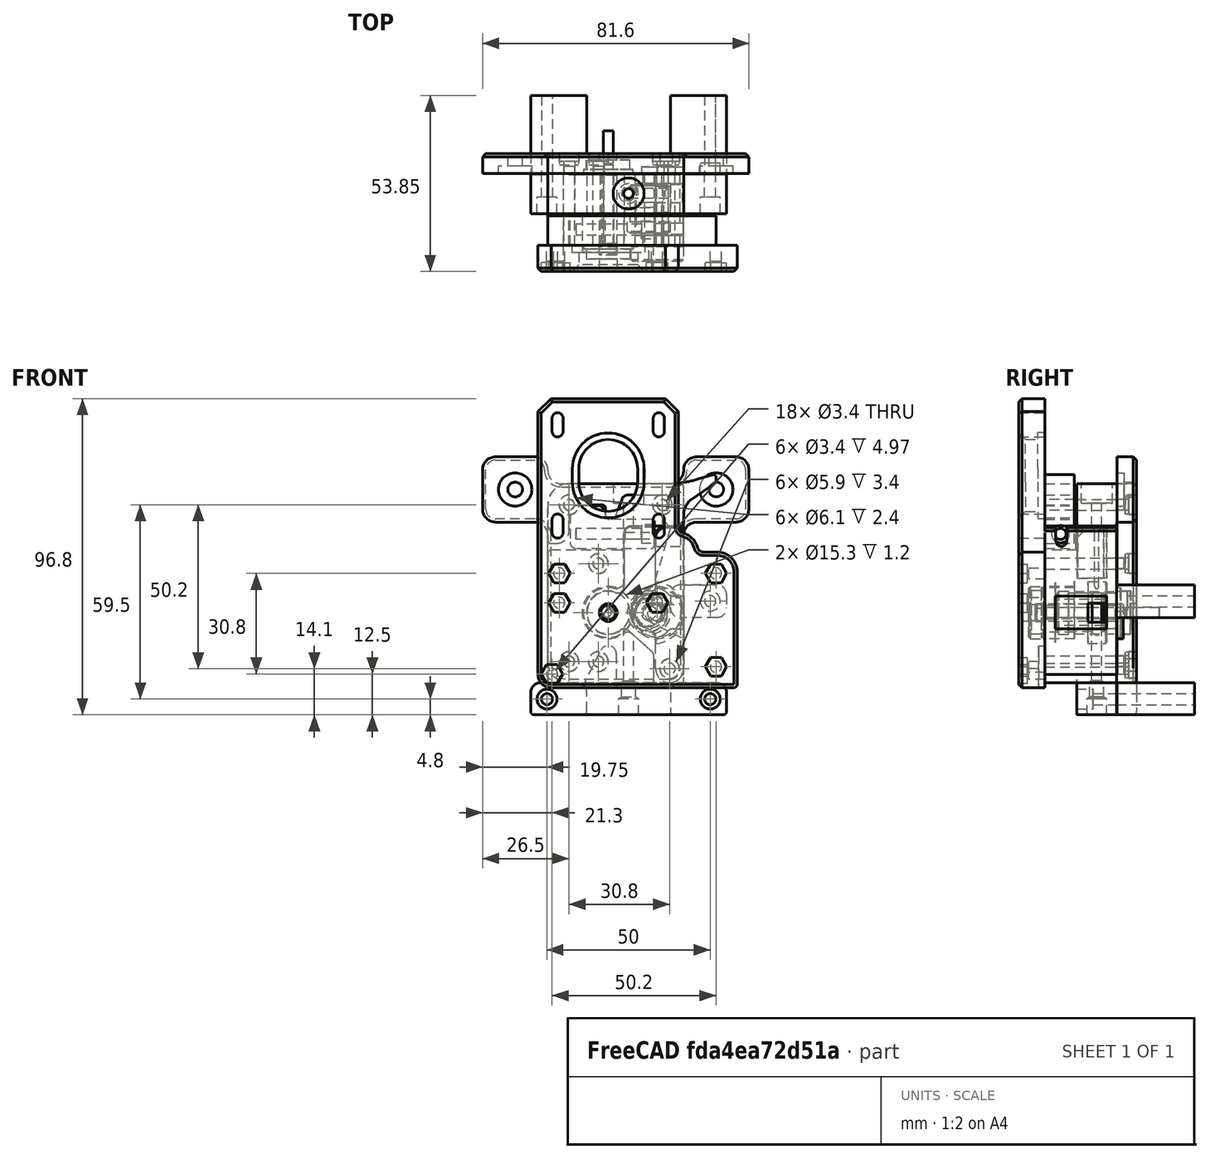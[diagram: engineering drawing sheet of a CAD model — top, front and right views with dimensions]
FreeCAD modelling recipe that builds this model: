
FCSTD DOCUMENT  (FreeCAD 1.0R39319 (Git))
Label: belted_extruder_v0.4
License: All rights reserved
LicenseURL: https://en.wikipedia.org/wiki/All_rights_reserved
objects: Sketcher::SketchObject×54, PartDesign::Fillet×34, PartDesign::Pad×26, PartDesign::Pocket×26, PartDesign::SubShapeBinder×15, PartDesign::Body×14, PartDesign::Hole×14, PartDesign::Chamfer×13, App::Part×13, App::DocumentObjectGroup×4, App::Link×4, App::FeaturePython×4, Mesh::Feature×2, PartDesign::Plane×2, PartDesign::Revolution×1, Spreadsheet::Sheet×1, PartDesign::FeatureBase×1, Assembly::JointGroup×1, Assembly::AssemblyObject×1
note: 483 computed .brp shape members not serialized (recipe doc carries the construction recipe); baked Part::Feature solids carry a one-line shape summary decoded from their .brp

FEATURE [Mesh::Feature] _0t_pulley_no_flange  label="60t_pulley_no_flange"
  Placement = pos=(0,-18,0) rot=(1,0,0;1.5708rad)
FEATURE [Mesh::Feature] _0t_pulley_no_flange001  label="80t_pulley_no_flange"
  Placement = pos=(0,-18,0) rot=(1,0,0;1.5708rad)
FEATURE [Sketcher::SketchObject] Sketch  label="base pulleys sketch"
  ArcFitTolerance = 1e-06
  FullyConstrained = true
  MakeInternals = false
  Placement = pos=(0,0,0) rot=(1,0,0;1.5708rad)
  sketch-geometry (12):
    g0: Circle CenterX=0 CenterY=0 CenterZ=0 NormalX=0 NormalY=0 NormalZ=1 AngleXU=0 Radius=25
    g1: Circle CenterX=-15.5 CenterY=59.5 CenterZ=0 NormalX=0 NormalY=0 NormalZ=1 AngleXU=0 Radius=1.7
    g2: Circle CenterX=15.5 CenterY=59.5 CenterZ=0 NormalX=0 NormalY=0 NormalZ=1 AngleXU=0 Radius=1.7
    g3: Circle CenterX=-15.5 CenterY=28.5 CenterZ=0 NormalX=0 NormalY=0 NormalZ=1 AngleXU=0 Radius=1.7
    g4: Circle CenterX=15.5 CenterY=28.5 CenterZ=0 NormalX=0 NormalY=0 NormalZ=1 AngleXU=0 Radius=1.7
    g5: LineSegment [constr] StartX=-15.5 StartY=59.5 StartZ=0 EndX=-15.5 EndY=28.5 EndZ=0
    g6: LineSegment [constr] StartX=-15.5 StartY=59.5 StartZ=0 EndX=15.5 EndY=59.5 EndZ=0
    g7: LineSegment [constr] StartX=15.5 StartY=59.5 StartZ=0 EndX=15.5 EndY=28.5 EndZ=0
    g8: LineSegment [constr] StartX=15.5 StartY=28.5 StartZ=0 EndX=-15.5 EndY=28.5 EndZ=0
    g9: LineSegment [constr] StartX=15.5 StartY=28.5 StartZ=0 EndX=-15.5 EndY=59.5 EndZ=0
    g10: Circle CenterX=3e-15 CenterY=44 CenterZ=0 NormalX=0 NormalY=0 NormalZ=1 AngleXU=0 Radius=9
    g11: Circle CenterX=0 CenterY=0 CenterZ=0 NormalX=0 NormalY=0 NormalZ=1 AngleXU=0 Radius=6
  constraints (27):
    c: Coincident(g0,g-1)
    c: Diameter(g0) = 50
    c: DistanceX(g1,g2) = 31
    c: DistanceY(g3,g1) = 31
    c: Coincident(g5,g1)
    c: Coincident(g5,g3)
    c: Vertical(g5)
    c: Coincident(g6,g1)
    c: Coincident(g6,g2)
    c: Coincident(g7,g2)
    c: Coincident(g7,g4)
    c: Vertical(g7)
    c: Coincident(g8,g4)
    c: Coincident(g8,g3)
    c: Horizontal(g8)
    c: Symmetric(g1,g2,g-2)
    c: Diameter(g2) = 3.4
    c: Equal(g2,g1)
    c: Equal(g3,g4)
    c: Equal(g3,g1)
    c: Coincident(g9,g4)
    c: Coincident(g9,g1)
    c: Symmetric(g9,g9,g10)
    c: Diameter(g10) = 18
    c: Coincident(g11,g0)
    c: Diameter(g11) = 12
    c: DistanceY(g0,g10) = 44
FEATURE [PartDesign::SubShapeBinder] Binder  label="base pulley binder"
  BindCopyOnChange = 0
  BindMode = 0
  ClaimChildren = false
  Context = -> Part [Body.Binder.]
  Fuse = false
  MakeFace = true
  OffsetFill = false
  OffsetIntersection = false
  OffsetJoinType = 0
  OffsetOpenResult = false
  PartialLoad = false
  Placement = pos=(0,0,0) rot=(0,-1,0;1.5708rad)
  Refine = true
  Relative = true
  Support = -> [Sketch]
  _Version = 2
FEATURE [Sketcher::SketchObject] Sketch006  label="filament path sketch"
  ArcFitTolerance = 1e-06
  FullyConstrained = true
  MakeInternals = false
  sketch-geometry (2):
    g0: Circle CenterX=6.25 CenterY=15.85 CenterZ=0 NormalX=0 NormalY=0 NormalZ=1 AngleXU=0 Radius=1.425
    g1: Circle CenterX=6.25 CenterY=15.85 CenterZ=0 NormalX=0 NormalY=0 NormalZ=1 AngleXU=0 Radius=5
  constraints (5):
    c: Diameter(g0) = 2.85
    c: DistanceX(g-1,g0) = 6.25
    c: DistanceY(g-1,g0) = 15.85
    c: Coincident(g1,g0)
    c: Diameter(g1) = 10
FEATURE [Sketcher::SketchObject] Sketch007
  ArcFitTolerance = 1e-06
  AttachmentSupport = -> [XY_Plane019]
  FullyConstrained = true
  MakeInternals = false
  MapMode = 5
  expr: Constraints[2] = 11.75 / 2
  expr: Constraints[6] = 13.25 / 2
  sketch-geometry (12):
    g0: LineSegment StartX=4 StartY=18.375 StartZ=0 EndX=5.875 EndY=18.375 EndZ=0
    g1: LineSegment [constr] StartX=0 StartY=18.375 StartZ=0 EndX=0 EndY=3.625 EndZ=0
    g2: LineSegment StartX=4 StartY=3.625 StartZ=0 EndX=6.625 EndY=3.625 EndZ=0
    g3: LineSegment StartX=6.625 StartY=3.625 StartZ=0 EndX=6.625 EndY=7.125 EndZ=0
    g4: LineSegment StartX=5.875 StartY=18.375 StartZ=0 EndX=5.875 EndY=17.375 EndZ=0
    g5: LineSegment [constr] StartX=5.875 StartY=17.375 StartZ=0 EndX=5.875 EndY=14.375 EndZ=0
    g6: LineSegment StartX=5.875 StartY=14.375 StartZ=0 EndX=5.875 EndY=7.125 EndZ=0
    g7: LineSegment StartX=5.875 StartY=7.125 StartZ=0 EndX=6.625 EndY=7.125 EndZ=0
    g8: ArcOfCircle CenterX=6.375 CenterY=15.875 CenterZ=0 NormalX=0 NormalY=0 NormalZ=1 AngleXU=0 Radius=1.58114 StartAngle=1.89255 EndAngle=4.39064
    g9: LineSegment StartX=4 StartY=18.375 StartZ=0 EndX=4 EndY=3.625 EndZ=0
    g10: LineSegment [constr] StartX=0 StartY=18.375 StartZ=0 EndX=4 EndY=18.375 EndZ=0
    g11: LineSegment [constr] StartX=0 StartY=3.625 StartZ=0 EndX=4 EndY=3.625 EndZ=0
  constraints (35):
    c: PointOnObject(g1,g-2)
    c: Horizontal(g0)
    c: DistanceX(g1,g0) = 5.875
    c: PointOnObject(g1,g-2)
    c: DistanceY(g1,g1) = 14.75
    c: Horizontal(g2)
    c: DistanceX(g1,g2) = 6.625
    c: Coincident(g3,g2)
    c: Vertical(g3)
    c: DistanceY(g3,g3) = 3.5
    c: Coincident(g4,g0)
    c: Vertical(g4)
    c: Coincident(g5,g4)
    c: Vertical(g5)
    c: DistanceY(g4,g4) = 1
    c: DistanceY(g5,g5) = 3
    c: Coincident(g6,g5)
    c: Vertical(g6)
    c: Coincident(g7,g6)
    c: Coincident(g7,g3)
    c: Horizontal(g7)
    c: DistanceY(g-1,g1) = 3.625
    c: Coincident(g8,g4)
    c: Coincident(g8,g5)
    c: DistanceX(g4,g8) = 0.5
    c: Vertical(g9)
    c: DistanceX(g1,g9) = 4
    c: Coincident(g0,g9)
    c: Coincident(g2,g9)
    c: Coincident(g10,g1)
    c: Coincident(g10,g0)
    c: Horizontal(g10)
    c: Coincident(g11,g1)
    c: Coincident(g11,g2)
    c: Horizontal(g11)
FEATURE [PartDesign::Revolution] Revolution
  Angle = 360
  Angle2 = 60
  Axis = (0,1,0)
  Base = (0,0,0)
  Profile = -> Sketch007
  ReferenceAxis = -> Sketch007 [V_Axis]
  Refine = true
  Reversed = true
  Suppressed = false
  Type = 0
FEATURE [PartDesign::Chamfer] Chamfer003
  Angle = 45
  Base = -> Revolution [Edge1,Edge2]
  BaseFeature = -> Revolution
  ChamferType = 0
  FlipDirection = false
  Refine = true
  Size = 0.25
  Size2 = 1
  SupportTransform = false
  Suppressed = false
  UseAllEdges = false
FEATURE [PartDesign::Chamfer] Chamfer004
  Angle = 45
  Base = -> Chamfer003 [Edge11]
  BaseFeature = -> Chamfer003
  ChamferType = 1
  FlipDirection = false
  Refine = true
  Size = 1
  Size2 = 0.5
  SupportTransform = false
  Suppressed = false
  UseAllEdges = false
FEATURE [PartDesign::Body] Body001  label="Drive Gear Body"
  AllowCompound = false
  Group = -> [Sketch007,Revolution,Chamfer003,Chamfer004]
  Origin = -> Origin019
  Tip = -> Chamfer004
FEATURE [PartDesign::SubShapeBinder] Binder003  label="filament path binder001"
  BindCopyOnChange = 0
  BindMode = 0
  ClaimChildren = false
  Context = -> Part003 [Body003.Binder003.]
  Fuse = false
  MakeFace = true
  OffsetFill = false
  OffsetIntersection = false
  OffsetJoinType = 0
  OffsetOpenResult = false
  PartialLoad = false
  Refine = true
  Relative = true
  Support = -> [Sketch006]
  _Version = 2
FEATURE [Sketcher::SketchObject] Sketch014  label="body screw placement"
  ArcFitTolerance = 1e-06
  FullyConstrained = true
  MakeInternals = false
  Placement = pos=(0,0,0) rot=(1,0,0;1.5708rad)
  sketch-geometry (15):
    g0: Circle CenterX=18.8 CenterY=-17.2 CenterZ=0 NormalX=0 NormalY=0 NormalZ=1 AngleXU=0 Radius=1.7
    g1: Circle CenterX=0 CenterY=33 CenterZ=0 NormalX=0 NormalY=0 NormalZ=1 AngleXU=0 Radius=1.7
    g2: Circle CenterX=-12 CenterY=33 CenterZ=0 NormalX=0 NormalY=0 NormalZ=1 AngleXU=0 Radius=1.7
    g3: Circle CenterX=-12 CenterY=-15 CenterZ=0 NormalX=0 NormalY=0 NormalZ=1 AngleXU=0 Radius=1.7
    g4: Circle [constr] CenterX=-12 CenterY=-15 CenterZ=0 NormalX=0 NormalY=0 NormalZ=1 AngleXU=0 Radius=2.75
    g5: Circle [constr] CenterX=0 CenterY=33 CenterZ=0 NormalX=0 NormalY=0 NormalZ=1 AngleXU=0 Radius=2.75
    g6: LineSegment [constr] StartX=-12 StartY=33 StartZ=0 EndX=0 EndY=33 EndZ=0
    g7: LineSegment [constr] StartX=-12 StartY=33 StartZ=0 EndX=-12 EndY=-15 EndZ=0
    g8: Circle CenterX=-3 CenterY=15 CenterZ=0 NormalX=0 NormalY=0 NormalZ=1 AngleXU=0 Radius=1.7
    g9: Circle CenterX=-3 CenterY=-15 CenterZ=0 NormalX=0 NormalY=0 NormalZ=1 AngleXU=0 Radius=1.7
    g10: LineSegment [constr] StartX=-3 StartY=-15 StartZ=0 EndX=-12 EndY=-15 EndZ=0
    g11: Circle CenterX=16.6 CenterY=33 CenterZ=0 NormalX=0 NormalY=0 NormalZ=1 AngleXU=0 Radius=1.7
    g12: LineSegment [constr] StartX=0 StartY=33 StartZ=0 EndX=16.6 EndY=33 EndZ=0
    g13: LineSegment [constr] StartX=18.8 StartY=-17.2 StartZ=0 EndX=18.8 EndY=33 EndZ=0
    g14: LineSegment [constr] StartX=16.6 StartY=33 StartZ=0 EndX=18.8 EndY=33 EndZ=0
  constraints (37):
    c: Diameter(g3) = 3.4
    c: Equal(g3,g2)
    c: Equal(g2,g1)
    c: Equal(g1,g0)
    c: Coincident(g4,g3)
    c: Diameter(g4) = 5.5
    c: Coincident(g5,g1)
    c: Diameter(g5) = 5.5
    c: Coincident(g6,g2)
    c: Coincident(g6,g1)
    c: Horizontal(g6)
    c: Coincident(g7,g2)
    c: Coincident(g7,g3)
    c: Vertical(g7)
    c: DistanceX(g2,g-1) = 12
    c: DistanceX(g-1,g0) = 18.8
    c: DistanceY(g-1,g2) = 33
    c: DistanceY(g3,g-1) = 15
    c: DistanceX(g-1,g1) = 0
    c: Coincident(g10,g9)
    c: Coincident(g10,g3)
    c: Horizontal(g10)
    c: Equal(g9,g3)
    c: Equal(g8,g9)
    c: DistanceY(g0,g9) = 2.2
    c: Symmetric(g9,g8,g-1)
    c: DistanceX(g8,g-1) = 3
    c: Coincident(g12,g1)
    c: Coincident(g12,g11)
    c: Horizontal(g12)
    c: Coincident(g13,g0)
    c: Vertical(g13)
    c: Coincident(g14,g11)
    c: Coincident(g14,g13)
    c: Horizontal(g14)
    c: DistanceX(g11,g13) = 2.2
    c: Equal(g3,g11)
FEATURE [PartDesign::SubShapeBinder] Binder004  label="tensioner axel binder"
  BindCopyOnChange = 0
  BindMode = 0
  ClaimChildren = false
  Context = -> Part003 [Body003.Binder004.]
  Fuse = false
  MakeFace = true
  OffsetFill = false
  OffsetIntersection = false
  OffsetJoinType = 0
  OffsetOpenResult = false
  PartialLoad = false
  Refine = true
  Relative = true
  Support = -> [Sketch014]
  _Version = 2
FEATURE [Sketcher::SketchObject] Sketch013  label="tensioner base sketch"
  ArcFitTolerance = 1e-06
  AttachmentSupport = -> [XZ_Plane022]
  ExternalGeometry = -> [Binder004]
  FullyConstrained = true
  MakeInternals = false
  MapMode = 5
  Placement = pos=(0,0,0) rot=(1,0,0;1.5708rad)
  sketch-geometry (15):
    g0: Circle [constr] CenterX=12.7 CenterY=0 CenterZ=0 NormalX=0 NormalY=0 NormalZ=1 AngleXU=0 Radius=4.5
    g1: LineSegment StartX=14.55 StartY=4.5 StartZ=0 EndX=14.55 EndY=26 EndZ=0
    g2: LineSegment StartX=14.55 StartY=26 StartZ=0 EndX=23.05 EndY=26 EndZ=0
    g3: Circle CenterX=12.7 CenterY=0 CenterZ=0 NormalX=0 NormalY=0 NormalZ=1 AngleXU=0 Radius=2.1
    g4: LineSegment StartX=14.55 StartY=-17.2 StartZ=0 EndX=14.55 EndY=-6.2 EndZ=0
    g5: LineSegment StartX=23.05 StartY=26 StartZ=0 EndX=23.05 EndY=-17.2 EndZ=0
    g6: LineSegment StartX=10.4965 StartY=-3.92361 StartZ=0 EndX=14.55 EndY=-6.2 EndZ=0
    g7: LineSegment [constr] StartX=14.55 StartY=-6.2 StartZ=0 EndX=14.55 EndY=4.5 EndZ=0
    g8: LineSegment StartX=14.55 StartY=4.5 StartZ=0 EndX=12.7 EndY=4.5 EndZ=0
    g9: ArcOfCircle CenterX=12.7 CenterY=0 CenterZ=0 NormalX=0 NormalY=0 NormalZ=1 AngleXU=0 Radius=4.5 StartAngle=1.5708 EndAngle=4.20069
    g10: Circle [constr] CenterX=12.7 CenterY=0 CenterZ=0 NormalX=0 NormalY=0 NormalZ=1 AngleXU=0 Radius=6
    g11: ArcOfCircle CenterX=18.8 CenterY=-17.2 CenterZ=0 NormalX=0 NormalY=0 NormalZ=1 AngleXU=0 Radius=4.25 StartAngle=3.14159 EndAngle=5.49779
    g12: ArcOfCircle [constr] CenterX=18.8 CenterY=-17.2 CenterZ=0 NormalX=0 NormalY=0 NormalZ=1 AngleXU=0 Radius=4.25 StartAngle=5.49779 EndAngle=6.28319
    g13: LineSegment StartX=23.05 StartY=-18.9604 StartZ=0 EndX=21.8052 EndY=-20.2052 EndZ=0
    g14: LineSegment StartX=23.05 StartY=-18.9604 StartZ=0 EndX=23.05 EndY=-17.2 EndZ=0
  constraints (36):
    c: PointOnObject(g0,g-1)
    c: Diameter(g0) = 9
    c: Vertical(g1)
    c: Coincident(g1,g2)
    c: Horizontal(g2)
    c: Coincident(g3,g0)
    c: Diameter(g3) = 4.2
    c: DistanceX(g-1,g0) = 12.7
    c: Coincident(g-4,g11)
    c: Tangent(g11,g4) = 1.5708
    c: Coincident(g5,g2)
    c: Vertical(g5)
    c: Tangent(g12,g5) = 1.5708
    c: Coincident(g6,g4)
    c: Coincident(g7,g4)
    c: Coincident(g7,g1)
    c: Vertical(g7)
    c: Vertical(g4)
    c: Coincident(g8,g1)
    c: Tangent(g8,g0) = -1.5708
    c: Horizontal(g8)
    c: Coincident(g9,g0)
    c: Coincident(g9,g8)
    c: Diameter(g10) = 12
    c: Coincident(g10,g0)
    c: Tangent(g6,g9) = -1.5708
    c: DistanceY(g11,g4) = 11
    c: Coincident(g11,g12)
    c: Coincident(g11,g12)
    c: Diameter(g11) = 8.5
    c: Angle(g5,g13) = 2.35619
    c: Tangent(g13,g11) = 1.5708
    c: Coincident(g14,g13)
    c: Coincident(g14,g5)
    c: Vertical(g14)
    c: DistanceY(g1,g-3) = 7
FEATURE [PartDesign::Pad] Pad003  label="tensioner base"
  Direction = (0,-1,2e-16)
  Length = 22
  Length2 = 10
  Placement = pos=(0,0,0) rot=(1,0,0;1.5708rad)
  Profile = -> Sketch013
  ReferenceAxis = -> Sketch013 [N_Axis]
  Refine = true
  Reversed = true
  Suppressed = false
  Type = 0
FEATURE [Sketcher::SketchObject] Sketch015
  ArcFitTolerance = 1e-06
  AttachmentSupport = -> [Pad003]
  ExternalGeometry = -> [Pad003]
  FullyConstrained = true
  MakeInternals = false
  MapMode = 5
  Placement = pos=(0,22,0) rot=(-1,0,0;1.5708rad)
  sketch-geometry (4):
    g0: ArcOfCircle CenterX=12.7 CenterY=4.9e-15 CenterZ=0 NormalX=0 NormalY=0 NormalZ=1 AngleXU=0 Radius=8 StartAngle=0.675132 EndAngle=5.60805
    g1: LineSegment StartX=18.945 StartY=5 StartZ=0 EndX=23.05 EndY=5 EndZ=0
    g2: LineSegment StartX=18.945 StartY=-5 StartZ=0 EndX=23.05 EndY=-5 EndZ=0
    g3: LineSegment StartX=23.05 StartY=5 StartZ=0 EndX=23.05 EndY=-5 EndZ=0
  constraints (11):
    c: Coincident(g0,g-3)
    c: Diameter(g0) = 16
    c: Horizontal(g1)
    c: Horizontal(g2)
    c: Symmetric(g2,g1,g-1)
    c: DistanceY(g2,g1) = 10
    c: Coincident(g0,g1)
    c: Coincident(g0,g2)
    c: Coincident(g3,g1)
    c: Coincident(g3,g2)
    c: PointOnObject(g2,g-4)
FEATURE [PartDesign::Pocket] Pocket005  label="tensioner pulley cutout"
  BaseFeature = -> Pad003
  Direction = (0,-1,-2e-16)
  Length = 18.9
  Length2 = -3.1
  Placement = pos=(0,0,0) rot=(1,0,0;1.5708rad)
  Profile = -> Sketch015
  ReferenceAxis = -> Sketch015 [N_Axis]
  Refine = true
  Suppressed = false
  Type = 4
FEATURE [PartDesign::SubShapeBinder] Binder006  label="body screws binder"
  BindCopyOnChange = 0
  BindMode = 0
  ClaimChildren = false
  Context = -> Part [Body.Binder006.]
  Fuse = false
  MakeFace = true
  OffsetFill = false
  OffsetIntersection = false
  OffsetJoinType = 0
  OffsetOpenResult = false
  PartialLoad = false
  Refine = true
  Relative = true
  Support = -> [Sketch014]
  _Version = 2
FEATURE [Sketcher::SketchObject] Sketch001
  ArcFitTolerance = 1e-06
  AttachmentSupport = -> [Binder]
  ExternalGeometry = -> [Binder,Binder006]
  FullyConstrained = true
  MakeInternals = false
  MapMode = 3
  Placement = pos=(0,0,0) rot=(0.57735,-0.57735,0.57735;2.0944rad)
  sketch-geometry (7):
    g0: LineSegment StartX=-23 StartY=21.5 StartZ=0 EndX=-23 EndY=-39.5 EndZ=0
    g1: LineSegment StartX=-23 StartY=-39.5 StartZ=0 EndX=18.5 EndY=-39.5 EndZ=0
    g2: LineSegment StartX=18.5 StartY=-39.5 StartZ=0 EndX=18.5 EndY=-21.5 EndZ=0
    g3: LineSegment StartX=18.5 StartY=-21.5 StartZ=0 EndX=65.5 EndY=-21.5 EndZ=0
    g4: LineSegment StartX=65.5 StartY=-21.5 StartZ=0 EndX=65.5 EndY=21.5 EndZ=0
    g5: LineSegment StartX=65.5 StartY=21.5 StartZ=0 EndX=-23 EndY=21.5 EndZ=0
    g6: Circle [constr] CenterX=44 CenterY=6.7e-15 CenterZ=0 NormalX=0 NormalY=0 NormalZ=1 AngleXU=0 Radius=21.5
  constraints (21):
    c: Vertical(g0)
    c: Coincident(g0,g1)
    c: Coincident(g1,g2)
    c: Vertical(g2)
    c: Coincident(g2,g3)
    c: Horizontal(g3)
    c: Coincident(g3,g4)
    c: Coincident(g4,g5)
    c: Coincident(g5,g0)
    c: Horizontal(g5)
    c: Symmetric(g4,g3,g-1)
    c: DistanceY(g4,g4) = 43
    c: Coincident(g6,g-3)
    c: Tangent(g6,g5)
    c: Tangent(g6,g4)
    c: DistanceX(g0,g-1) = 23
    c: Perpendicular(g2,g1)
    c: DistanceX(g-6,g1) = 6.5
    c: DistanceY(g1,g-6) = 6.5
    c: DistanceX(g-1,g6) = 44
    c: DistanceY(g2,g2) = 18
FEATURE [PartDesign::Pad] Pad
  Direction = (0,-1,0)
  Length = 8
  Length2 = 10
  Placement = pos=(0,0,0) rot=(0,-1,0;1.5708rad)
  Profile = -> Sketch001
  ReferenceAxis = -> Sketch001 [N_Axis]
  Refine = true
  Suppressed = false
  Type = 0
FEATURE [Sketcher::SketchObject] Sketch002  label="motor cutouts"
  ArcFitTolerance = 1e-06
  AttachmentSupport = -> [Pad]
  ExternalGeometry = -> [Binder]
  FullyConstrained = true
  MakeInternals = false
  MapMode = 5
  Placement = pos=(0,0,0) rot=(0.57735,-0.57735,-0.57735;4.18879rad)
  sketch-geometry (29):
    g0: ArcOfCircle CenterX=-44 CenterY=6.7e-15 CenterZ=0 NormalX=0 NormalY=0 NormalZ=1 AngleXU=0 Radius=9 StartAngle=1.5708 EndAngle=4.71239
    g1: LineSegment StartX=-44 StartY=9 StartZ=0 EndX=-40 EndY=9 EndZ=0
    g2: LineSegment StartX=-44 StartY=-9 StartZ=0 EndX=-40 EndY=-9 EndZ=0
    g3: LineSegment [constr] StartX=-44 StartY=-9 StartZ=0 EndX=-44 EndY=9 EndZ=0
    g4: ArcOfCircle CenterX=-40 CenterY=7.1e-15 CenterZ=0 NormalX=0 NormalY=0 NormalZ=1 AngleXU=0 Radius=9 StartAngle=4.71239 EndAngle=7.85398
    g5: ArcOfCircle CenterX=-59.5 CenterY=15.5 CenterZ=0 NormalX=0 NormalY=0 NormalZ=1 AngleXU=0 Radius=1.7 StartAngle=1.5708 EndAngle=4.71239
    g6: ArcOfCircle CenterX=-59.5 CenterY=-15.5 CenterZ=0 NormalX=0 NormalY=0 NormalZ=1 AngleXU=0 Radius=1.7 StartAngle=1.5708 EndAngle=4.71239
    g7: ArcOfCircle CenterX=-28.5 CenterY=-15.5 CenterZ=0 NormalX=0 NormalY=0 NormalZ=1 AngleXU=0 Radius=1.7 StartAngle=1.5708 EndAngle=4.71238
    g8: ArcOfCircle CenterX=-28.5 CenterY=15.5 CenterZ=0 NormalX=0 NormalY=0 NormalZ=1 AngleXU=0 Radius=1.7 StartAngle=1.5708 EndAngle=4.71239
    g9: LineSegment StartX=-59.5 StartY=13.8 StartZ=0 EndX=-55.5 EndY=13.8 EndZ=0
    g10: LineSegment StartX=-59.5 StartY=17.2 StartZ=0 EndX=-55.5 EndY=17.2 EndZ=0
    g11: LineSegment [constr] StartX=-59.5 StartY=17.2 StartZ=0 EndX=-59.5 EndY=13.8 EndZ=0
    g12: LineSegment [constr] StartX=-55.5 StartY=17.2 StartZ=0 EndX=-55.5 EndY=13.8 EndZ=0
    g13: ArcOfCircle CenterX=-55.5 CenterY=15.5 CenterZ=0 NormalX=0 NormalY=0 NormalZ=1 AngleXU=0 Radius=1.7 StartAngle=4.71239 EndAngle=7.85398
    g14: LineSegment StartX=-59.5 StartY=-13.8 StartZ=0 EndX=-55.5 EndY=-13.8 EndZ=0
    g15: LineSegment StartX=-59.5 StartY=-17.2 StartZ=0 EndX=-55.5 EndY=-17.2 EndZ=0
    g16: LineSegment [constr] StartX=-59.5 StartY=-13.8 StartZ=0 EndX=-59.5 EndY=-17.2 EndZ=0
    g17: LineSegment [constr] StartX=-55.5 StartY=-13.8 StartZ=0 EndX=-55.5 EndY=-17.2 EndZ=0
    g18: ArcOfCircle CenterX=-55.5 CenterY=-15.5 CenterZ=0 NormalX=0 NormalY=0 NormalZ=1 AngleXU=0 Radius=1.7 StartAngle=4.71238 EndAngle=7.85399
    g19: LineSegment StartX=-28.5 StartY=-17.2 StartZ=0 EndX=-24.5 EndY=-17.2 EndZ=0
    g20: LineSegment StartX=-28.5 StartY=-13.8 StartZ=0 EndX=-24.5 EndY=-13.8 EndZ=0
    g21: LineSegment [constr] StartX=-28.5 StartY=-13.8 StartZ=0 EndX=-28.5 EndY=-17.2 EndZ=0
    g22: LineSegment [constr] StartX=-24.5 StartY=-13.8 StartZ=0 EndX=-24.5 EndY=-17.2 EndZ=0
    g23: ArcOfCircle CenterX=-24.5 CenterY=-15.5 CenterZ=0 NormalX=0 NormalY=0 NormalZ=1 AngleXU=0 Radius=1.7 StartAngle=4.71239 EndAngle=7.85398
    g24: LineSegment StartX=-28.5 StartY=13.8 StartZ=0 EndX=-24.5 EndY=13.8 EndZ=0
    g25: LineSegment StartX=-28.5 StartY=17.2 StartZ=0 EndX=-24.5 EndY=17.2 EndZ=0
    g26: LineSegment [constr] StartX=-24.5 StartY=17.2 StartZ=0 EndX=-24.5 EndY=13.8 EndZ=0
    g27: LineSegment [constr] StartX=-28.5 StartY=17.2 StartZ=0 EndX=-28.5 EndY=13.8 EndZ=0
    g28: ArcOfCircle CenterX=-24.5 CenterY=15.5 CenterZ=0 NormalX=0 NormalY=0 NormalZ=1 AngleXU=0 Radius=1.7 StartAngle=4.71239 EndAngle=7.85398
  constraints (76):
    c: Coincident(g0,g-3)
    c: Equal(g0,g-3)
    c: Horizontal(g1)
    c: Horizontal(g2)
    c: Coincident(g3,g2)
    c: Coincident(g3,g1)
    c: Vertical(g3)
    c: DistanceX(g2,g2) = 4
    c: Coincident(g0,g1)
    c: Tangent(g0,g2) = -1.5708
    c: Coincident(g4,g1)
    c: Equal(g5,g-4)
    c: Equal(g2,g1)
    c: Coincident(g5,g-4)
    c: Coincident(g6,g-5)
    c: Coincident(g7,g-7)
    c: Equal(g-5,g6)
    c: Equal(g7,g-7)
    c: Horizontal(g9)
    c: Coincident(g11,g10)
    c: Coincident(g11,g9)
    c: Vertical(g11)
    c: Coincident(g12,g10)
    c: Coincident(g12,g9)
    c: Vertical(g12)
    c: DistanceX(g9,g9) = 4
    c: Equal(g12,g11)
    c: Symmetric(g12,g12,g13)
    c: Coincident(g13,g10)
    c: Coincident(g5,g9)
    c: Tangent(g5,g10) = 1.5708
    c: Horizontal(g14)
    c: Horizontal(g15)
    c: Coincident(g16,g14)
    c: Coincident(g16,g15)
    c: Coincident(g17,g14)
    c: Coincident(g17,g15)
    c: Vertical(g17)
    c: Vertical(g16)
    c: DistanceX(g15,g15) = 4
    c: Tangent(g6,g14) = 1.5708
    c: Coincident(g6,g15)
    c: Coincident(g18,g14)
    c: Angle(g13) = 3.14159
    c: Horizontal(g19)
    c: Horizontal(g20)
    c: Coincident(g21,g20)
    c: Coincident(g21,g19)
    c: Coincident(g7,g19)
    c: Coincident(g22,g20)
    c: Coincident(g22,g19)
    c: Vertical(g22)
    c: DistanceX(g19,g19) = 4
    c: Coincident(g23,g19)
    c: Equal(g23,g7)
    c: Coincident(g4,g2)
    c: Equal(g4,g0)
    c: Equal(g18,g6)
    c: Coincident(g18,g15)
    c: Horizontal(g24)
    c: Horizontal(g25)
    c: Coincident(g26,g25)
    c: Coincident(g26,g24)
    c: Coincident(g27,g25)
    c: Coincident(g27,g24)
    c: DistanceX(g24,g24) = 4
    c: Coincident(g8,g24)
    c: Tangent(g8,g25) = 1.5708
    c: Coincident(g28,g25)
    c: Vertical(g26)
    c: Coincident(g8,g-6)
    c: Equal(g8,g-6)
    c: Vertical(g27)
    c: Tangent(g28,g24) = -1.5708
    c: Tangent(g23,g20) = 1.5708
    c: Tangent(g20,g7) = 1.5708
FEATURE [PartDesign::Pocket] Pocket
  BaseFeature = -> Pad
  Direction = (0,-1,0)
  Length = 0
  Length2 = 5
  Placement = pos=(0,0,0) rot=(0,-1,0;1.5708rad)
  Profile = -> Sketch002
  ReferenceAxis = -> Sketch002 [N_Axis]
  Refine = true
  Suppressed = false
  Type = 3
  UpToFace = -> Pad [Face8]
FEATURE [Sketcher::SketchObject] Sketch003
  ArcFitTolerance = 1e-06
  AttachmentSupport = -> [Pocket]
  FullyConstrained = true
  MakeInternals = false
  MapMode = 5
  Placement = pos=(0,0,0) rot=(0.57735,-0.57735,-0.57735;4.18879rad)
  sketch-geometry (1):
    g0: Circle CenterX=0 CenterY=0 CenterZ=0 NormalX=0 NormalY=0 NormalZ=1 AngleXU=0 Radius=6.45
  constraints (2):
    c: Coincident(g0,g-1)
    c: Diameter(g0) = 12.9
FEATURE [PartDesign::Hole] Hole
  BaseFeature = -> Pocket
  CustomThreadClearance = 0
  Depth = 4.2
  DepthType = 0
  Diameter = 13.3
  DrillForDepth = false
  DrillPoint = 0
  DrillPointAngle = 118
  HoleCutCountersinkAngle = 90
  HoleCutCustomValues = false
  HoleCutDepth = 1.2
  HoleCutDiameter = 15.3
  HoleCutType = 1
  ModelThread = false
  Placement = pos=(0,0,0) rot=(0,-1,0;1.5708rad)
  Profile = -> Sketch003
  Refine = true
  Suppressed = false
  Tapered = false
  TaperedAngle = 90
  ThreadClass = 0
  ThreadDepth = 4.2
  ThreadDepthType = 0
  ThreadDirection = 0
  ThreadFit = 0
  ThreadSize = 0
  ThreadType = 0
  Threaded = false
  UseCustomThreadClearance = false
FEATURE [PartDesign::Hole] Hole001  label="Bearign Hole"
  BaseFeature = -> Hole
  CustomThreadClearance = 0
  Depth = 25
  DepthType = 0
  Diameter = 5.4
  DrillForDepth = false
  DrillPoint = 1
  DrillPointAngle = 118
  HoleCutCountersinkAngle = 90
  HoleCutCustomValues = false
  HoleCutDepth = 0
  HoleCutDiameter = 6.1
  HoleCutType = 0
  ModelThread = false
  Placement = pos=(0,0,0) rot=(0,-1,0;1.5708rad)
  Profile = -> Hole [Face32]
  Refine = true
  Suppressed = false
  Tapered = false
  TaperedAngle = 90
  ThreadClass = 0
  ThreadDepth = 25
  ThreadDepthType = 0
  ThreadDirection = 0
  ThreadFit = 0
  ThreadSize = 0
  ThreadType = 0
  Threaded = false
  UseCustomThreadClearance = false
FEATURE [Sketcher::SketchObject] Sketch004
  ArcFitTolerance = 1e-06
  AttachmentSupport = -> [Pocket]
  ExternalGeometry = -> [Binder006]
  FullyConstrained = true
  MakeInternals = false
  MapMode = 5
  Placement = pos=(0,0,0) rot=(0.57735,-0.57735,-0.57735;4.18879rad)
  sketch-geometry (1):
    g0: Circle CenterX=18.8 CenterY=17.2 CenterZ=0 NormalX=0 NormalY=0 NormalZ=1 AngleXU=0 Radius=1.6
  constraints (2):
    c: Coincident(g0,g-3)
    c: Diameter(g0) = 3.2
FEATURE [PartDesign::Pocket] Pocket001
  BaseFeature = -> Hole001
  Direction = (0,-1,0)
  Length = 10
  Length2 = 5
  Placement = pos=(0,0,0) rot=(0,-1,0;1.5708rad)
  Profile = -> Sketch004
  ReferenceAxis = -> Sketch004 [N_Axis]
  Refine = true
  Suppressed = false
  Type = 0
FEATURE [Sketcher::SketchObject] Sketch005  label="corner reinforcemtn"
  ArcFitTolerance = 1e-06
  AttachmentSupport = -> [Pocket001]
  ExternalGeometry = -> [Pocket001]
  FullyConstrained = true
  MakeInternals = false
  MapMode = 5
  Placement = pos=(0,0,0) rot=(0.57735,-0.57735,-0.57735;4.18879rad)
  sketch-geometry (3):
    g0: ArcOfCircle CenterX=-18.5 CenterY=-21.5 CenterZ=0 NormalX=0 NormalY=0 NormalZ=1 AngleXU=0 Radius=6 StartAngle=3.14159 EndAngle=4.71239
    g1: LineSegment StartX=-24.5 StartY=-21.5 StartZ=0 EndX=-18.5 EndY=-21.5 EndZ=0
    g2: LineSegment StartX=-18.5 StartY=-21.5 StartZ=0 EndX=-18.5 EndY=-27.5 EndZ=0
  constraints (8):
    c: PointOnObject(g0,g-3)
    c: Coincident(g1,g0)
    c: Coincident(g1,g0)
    c: Coincident(g2,g0)
    c: Coincident(g2,g0)
    c: Radius(g0) = 6
    c: Coincident(g0,g-4)
    c: Vertical(g2)
FEATURE [PartDesign::Pad] Pad001  label="reinforcement"
  BaseFeature = -> Pocket001
  Direction = (0,1,0)
  Length = 10
  Length2 = 10
  Placement = pos=(0,0,0) rot=(0,-1,0;1.5708rad)
  Profile = -> Sketch005
  ReferenceAxis = -> Sketch005 [N_Axis]
  Refine = true
  Reversed = true
  Suppressed = false
  Type = 3
  UpToFace = -> Pocket001 [Face5]
FEATURE [PartDesign::Fillet] Fillet
  Base = -> Pad001 [Edge19,Edge15]
  BaseFeature = -> Pad001
  Placement = pos=(0,0,0) rot=(0,-1,0;1.5708rad)
  Radius = 2
  Refine = true
  SupportTransform = false
  Suppressed = false
  UseAllEdges = false
FEATURE [PartDesign::Chamfer] Chamfer
  Angle = 45
  Base = -> Fillet [Edge70,Edge68]
  BaseFeature = -> Fillet
  ChamferType = 0
  FlipDirection = false
  Placement = pos=(0,0,0) rot=(0,-1,0;1.5708rad)
  Refine = true
  Size = 4
  Size2 = 1
  SupportTransform = false
  Suppressed = false
  UseAllEdges = false
FEATURE [Sketcher::SketchObject] Sketch016  label="tensioner screw sketch"
  ArcFitTolerance = 1e-06
  AttachmentSupport = -> [Pocket005]
  FullyConstrained = true
  MakeInternals = false
  MapMode = 5
  Placement = pos=(23.05,0,0) rot=(0.707107,0,0.707107;3.14159rad)
  sketch-geometry (5):
    g0: ArcOfCircle CenterX=24 CenterY=-4.9 CenterZ=0 NormalX=0 NormalY=0 NormalZ=1 AngleXU=0 Radius=1.8 StartAngle=1.5708 EndAngle=4.71239
    g1: LineSegment StartX=24 StartY=-3.1 StartZ=0 EndX=30 EndY=-3.1 EndZ=0
    g2: LineSegment StartX=24 StartY=-6.7 StartZ=0 EndX=30 EndY=-6.7 EndZ=0
    g3: ArcOfCircle CenterX=30 CenterY=-4.9 CenterZ=0 NormalX=0 NormalY=0 NormalZ=1 AngleXU=0 Radius=1.8 StartAngle=4.71239 EndAngle=7.85398
    g4: LineSegment [constr] StartX=24 StartY=-4.9 StartZ=0 EndX=30 EndY=-4.9 EndZ=0
  constraints (14):
    c: Diameter(g0) = 3.6
    c: Horizontal(g2)
    c: Horizontal(g1)
    c: DistanceX(g-1,g0) = 24
    c: Coincident(g3,g1)
    c: Coincident(g3,g2)
    c: Coincident(g4,g0)
    c: Coincident(g4,g3)
    c: Horizontal(g4)
    c: Equal(g0,g3)
    c: Tangent(g0,g1) = 1.5708
    c: Tangent(g0,g2) = -1.5708
    c: DistanceX(g4,g4) = 6
    c: DistanceY(g3,g-1) = 4.9
FEATURE [Sketcher::SketchObject] Sketch017
  ArcFitTolerance = 1e-06
  ExternalGeometry = -> [Binder004]
  FullyConstrained = true
  MakeInternals = false
  MapMode = 5
  Placement = pos=(0,6e-16,0) rot=(1,0,0;1.5708rad)
  sketch-geometry (1):
    g0: Circle CenterX=18.8 CenterY=-17.2 CenterZ=0 NormalX=0 NormalY=0 NormalZ=1 AngleXU=0 Radius=1.7
  constraints (2):
    c: Coincident(g0,g-3)
    c: Equal(g0,g-3)
FEATURE [PartDesign::Hole] Hole003  label="tensioner axle"
  BaseFeature = -> Pocket005
  CustomThreadClearance = 0
  Depth = 25
  DepthType = 0
  Diameter = 3.4
  DrillForDepth = false
  DrillPoint = 1
  DrillPointAngle = 118
  HoleCutCountersinkAngle = 90
  HoleCutCustomValues = false
  HoleCutDepth = 0
  HoleCutDiameter = 6.1
  HoleCutType = 0
  ModelThread = false
  Placement = pos=(0,0,0) rot=(1,0,0;1.5708rad)
  Profile = -> Sketch017
  Refine = true
  Suppressed = false
  Tapered = false
  TaperedAngle = 90
  ThreadClass = 0
  ThreadDepth = 25
  ThreadDepthType = 0
  ThreadDirection = 0
  ThreadFit = 0
  ThreadSize = 0
  ThreadType = 0
  Threaded = false
  UseCustomThreadClearance = false
FEATURE [Sketcher::SketchObject] Sketch018
  ArcFitTolerance = 1e-06
  AttachmentSupport = -> [Hole003]
  ExternalGeometry = -> [Hole003]
  FullyConstrained = true
  MakeInternals = false
  MapMode = 5
  Placement = pos=(0,6e-16,0) rot=(1,0,0;1.5708rad)
  sketch-geometry (3):
    g0: LineSegment StartX=19.05 StartY=26 StartZ=0 EndX=14.55 EndY=10.5 EndZ=0
    g1: LineSegment StartX=14.55 StartY=10.5 StartZ=0 EndX=14.55 EndY=26 EndZ=0
    g2: LineSegment StartX=14.55 StartY=26 StartZ=0 EndX=19.05 EndY=26 EndZ=0
  constraints (8):
    c: PointOnObject(g0,g-4)
    c: PointOnObject(g0,g-3)
    c: DistanceX(g0,g-4) = 4
    c: DistanceY(g-3,g0) = 6
    c: Coincident(g1,g0)
    c: Coincident(g1,g-4)
    c: Coincident(g2,g1)
    c: Coincident(g2,g0)
FEATURE [PartDesign::Pocket] Pocket007  label="finger tab cutout"
  BaseFeature = -> Hole003
  Direction = (0,1,-2e-16)
  Length = 18
  Length2 = -10
  Placement = pos=(0,0,0) rot=(1,0,0;1.5708rad)
  Profile = -> Sketch018
  ReferenceAxis = -> Sketch018 [N_Axis]
  Refine = true
  Suppressed = false
  Type = 4
FEATURE [PartDesign::Chamfer] Chamfer002  label="Motor Axle Cutout"
  Angle = 45
  Base = -> Chamfer [Edge60,Edge59,Edge58,Edge61,Edge57,Edge63]
  BaseFeature = -> Chamfer
  ChamferType = 0
  FlipDirection = false
  Placement = pos=(0,0,0) rot=(0,-1,0;1.5708rad)
  Refine = true
  Size = 2
  Size2 = 1
  SupportTransform = false
  Suppressed = false
  UseAllEdges = false
FEATURE [Sketcher::SketchObject] Sketch023
  ArcFitTolerance = 1e-06
  AttachmentSupport = -> [Chamfer002]
  ExternalGeometry = -> [Sketch004,Chamfer002]
  FullyConstrained = true
  MakeInternals = false
  MapMode = 5
  Placement = pos=(0,0,0) rot=(0.57735,-0.57735,-0.57735;4.18879rad)
  sketch-geometry (5):
    g0: Circle [constr] CenterX=12.666 CenterY=0 CenterZ=0 NormalX=0 NormalY=0 NormalZ=1 AngleXU=0 Radius=2.5
    g1: LineSegment StartX=23 StartY=8 StartZ=0 EndX=11.5421 EndY=2.2331 EndZ=0
    g2: LineSegment StartX=12.666 StartY=-2.5 StartZ=0 EndX=23 EndY=-2.5 EndZ=0
    g3: ArcOfCircle CenterX=12.666 CenterY=0 CenterZ=0 NormalX=0 NormalY=0 NormalZ=1 AngleXU=0 Radius=2.5 StartAngle=2.03709 EndAngle=4.71239
    g4: LineSegment StartX=23 StartY=8 StartZ=0 EndX=23 EndY=-2.5 EndZ=0
  constraints (13):
    c: PointOnObject(g0,g-1)
    c: DistanceX(g-1,g0) = 12.666
    c: Tangent(g2,g0) = -1.5708
    c: PointOnObject(g2,g-3)
    c: Horizontal(g2)
    c: Diameter(g0) = 5
    c: Coincident(g3,g0)
    c: Coincident(g3,g2)
    c: Tangent(g3,g1) = -1.5708
    c: PointOnObject(g4,g-3)
    c: Coincident(g4,g2)
    c: Coincident(g1,g4)
    c: DistanceY(g4,g4) = 10.5
FEATURE [PartDesign::Pocket] Pocket009  label="Tensioner Axle Cutout"
  BaseFeature = -> Chamfer002
  Direction = (0,-1,0)
  Length = 2
  Length2 = 5
  Placement = pos=(0,0,0) rot=(0,-1,0;1.5708rad)
  Profile = -> Sketch023
  ReferenceAxis = -> Sketch023 [N_Axis]
  Refine = true
  Suppressed = false
  Type = 0
FEATURE [Sketcher::SketchObject] Sketch025  label="Extruder Screw Holes"
  ArcFitTolerance = 1e-06
  ExternalGeometry = -> [Binder006]
  FullyConstrained = true
  MakeInternals = false
  MapMode = 5
  Placement = pos=(0,0,0) rot=(0.57735,-0.57735,-0.57735;4.18879rad)
  sketch-geometry (6):
    g0: Circle CenterX=-12 CenterY=15 CenterZ=0 NormalX=0 NormalY=0 NormalZ=1 AngleXU=0 Radius=1.7
    g1: Circle CenterX=-3 CenterY=15 CenterZ=0 NormalX=0 NormalY=0 NormalZ=1 AngleXU=0 Radius=1.7
    g2: Circle CenterX=-3 CenterY=-15 CenterZ=0 NormalX=0 NormalY=0 NormalZ=1 AngleXU=0 Radius=1.7
    g3: Circle CenterX=-12 CenterY=-33 CenterZ=0 NormalX=0 NormalY=0 NormalZ=1 AngleXU=0 Radius=1.7
    g4: Circle CenterX=16.6 CenterY=-33 CenterZ=0 NormalX=0 NormalY=0 NormalZ=1 AngleXU=0 Radius=1.7
    g5: Circle CenterX=18.8 CenterY=17.2 CenterZ=0 NormalX=0 NormalY=0 NormalZ=1 AngleXU=0 Radius=1.7
  constraints (12):
    c: Coincident(g0,g-4)
    c: Equal(g0,g-4)
    c: Coincident(g1,g-6)
    c: Equal(g1,g-6)
    c: Coincident(g2,g-5)
    c: Equal(g2,g-5)
    c: Coincident(g3,g-3)
    c: Equal(g3,g-3)
    c: Coincident(g5,g-7)
    c: Diameter(g5) = 3.4
    c: Coincident(g4,g-9)
    c: Equal(g4,g-9)
FEATURE [PartDesign::Pocket] Pocket013  label="Extruder Holes"
  BaseFeature = -> Pocket009
  Direction = (-2e-16,-1,-2e-16)
  Length = 0
  Length2 = 5
  Placement = pos=(0,0,0) rot=(0,-1,0;1.5708rad)
  Profile = -> Sketch025
  ReferenceAxis = -> Sketch025 [N_Axis]
  Refine = true
  Suppressed = false
  Type = 3
  UpToFace = -> Pocket009 [Face9]
FEATURE [Spreadsheet::Sheet] Spreadsheet  label="Dimensions"
  cells = A2='M3 Hex Insert Width; B2(M3HexW)=5.7; A3='M3 Hex Insert Depth; B3(M3HexD)=2.63; A4='M3 Heat Set Width; B4(M3HeatSetW)=5.5; A5='M3 Heat Set Depth; B5(M3HeatSetD)=4; A6='M3 Cap Width; B6(M3Cap)=5.9
FEATURE [Sketcher::SketchObject] Sketch026
  ArcFitTolerance = 1e-06
  AttachmentSupport = -> [Pocket013]
  ExternalGeometry = -> [Pocket013]
  FullyConstrained = true
  MakeInternals = false
  MapMode = 5
  Placement = pos=(0,-8,0) rot=(0.57735,-0.57735,0.57735;2.0944rad)
  expr: Constraints[90] = <<Dimensions>>.M3HexW
  expr: Constraints[97] = <<Dimensions>>.M3HexW
  sketch-geometry (42):
    g0: LineSegment StartX=0.15 StartY=13.3546 StartZ=0 EndX=3 EndY=11.7091 EndZ=0
    g1: LineSegment StartX=3 StartY=11.7091 StartZ=0 EndX=5.85 EndY=13.3546 EndZ=0
    g2: LineSegment StartX=5.85 StartY=13.3546 StartZ=0 EndX=5.85 EndY=16.6454 EndZ=0
    g3: LineSegment StartX=5.85 StartY=16.6454 StartZ=0 EndX=3 EndY=18.2909 EndZ=0
    g4: LineSegment StartX=3 StartY=18.2909 StartZ=0 EndX=0.15 EndY=16.6454 EndZ=0
    g5: LineSegment StartX=0.15 StartY=16.6454 StartZ=0 EndX=0.15 EndY=13.3546 EndZ=0
    g6: Circle [constr] CenterX=3 CenterY=15 CenterZ=0 NormalX=0 NormalY=0 NormalZ=1 AngleXU=0 Radius=3.2909
    g7: LineSegment StartX=9.15 StartY=13.3546 StartZ=0 EndX=12 EndY=11.7091 EndZ=0
    g8: LineSegment StartX=12 StartY=11.7091 StartZ=0 EndX=14.85 EndY=13.3546 EndZ=0
    g9: LineSegment StartX=14.85 StartY=13.3546 StartZ=0 EndX=14.85 EndY=16.6454 EndZ=0
    g10: LineSegment StartX=14.85 StartY=16.6454 StartZ=0 EndX=12 EndY=18.2909 EndZ=0
    g11: LineSegment StartX=12 StartY=18.2909 StartZ=0 EndX=9.15 EndY=16.6454 EndZ=0
    g12: LineSegment StartX=9.15 StartY=16.6454 StartZ=0 EndX=9.15 EndY=13.3546 EndZ=0
    g13: Circle [constr] CenterX=12 CenterY=15 CenterZ=0 NormalX=0 NormalY=0 NormalZ=1 AngleXU=0 Radius=3.2909
    g14: LineSegment StartX=3 StartY=-18.2909 StartZ=0 EndX=5.85 EndY=-16.6454 EndZ=0
    g15: LineSegment StartX=5.85 StartY=-16.6454 StartZ=0 EndX=5.85 EndY=-13.3546 EndZ=0
    g16: LineSegment StartX=5.85 StartY=-13.3546 StartZ=0 EndX=3 EndY=-11.7091 EndZ=0
    g17: LineSegment StartX=3 StartY=-11.7091 StartZ=0 EndX=0.15 EndY=-13.3546 EndZ=0
    g18: LineSegment StartX=0.15 StartY=-13.3546 StartZ=0 EndX=0.15 EndY=-16.6454 EndZ=0
    g19: LineSegment StartX=0.15 StartY=-16.6454 StartZ=0 EndX=3 EndY=-18.2909 EndZ=0
    g20: Circle [constr] CenterX=3 CenterY=-15 CenterZ=0 NormalX=0 NormalY=0 NormalZ=1 AngleXU=0 Radius=3.2909
    g21: LineSegment StartX=-19.45 StartY=-34.6454 StartZ=0 EndX=-16.6 EndY=-36.2909 EndZ=0
    g22: LineSegment StartX=-16.6 StartY=-36.2909 StartZ=0 EndX=-13.75 EndY=-34.6454 EndZ=0
    g23: LineSegment StartX=-13.75 StartY=-34.6454 StartZ=0 EndX=-13.75 EndY=-31.3546 EndZ=0
    g24: LineSegment StartX=-13.75 StartY=-31.3546 StartZ=0 EndX=-16.6 EndY=-29.7091 EndZ=0
    g25: LineSegment StartX=-16.6 StartY=-29.7091 StartZ=0 EndX=-19.45 EndY=-31.3546 EndZ=0
    g26: LineSegment StartX=-19.45 StartY=-31.3546 StartZ=0 EndX=-19.45 EndY=-34.6454 EndZ=0
    g27: Circle [constr] CenterX=-16.6 CenterY=-33 CenterZ=0 NormalX=0 NormalY=0 NormalZ=1 AngleXU=0 Radius=3.2909
    g28: LineSegment StartX=9.15 StartY=-34.6454 StartZ=0 EndX=12 EndY=-36.2909 EndZ=0
    g29: LineSegment StartX=12 StartY=-36.2909 StartZ=0 EndX=14.85 EndY=-34.6454 EndZ=0
    g30: LineSegment StartX=14.85 StartY=-34.6454 StartZ=0 EndX=14.85 EndY=-31.3546 EndZ=0
    g31: LineSegment StartX=14.85 StartY=-31.3546 StartZ=0 EndX=12 EndY=-29.7091 EndZ=0
    g32: LineSegment StartX=12 StartY=-29.7091 StartZ=0 EndX=9.15 EndY=-31.3546 EndZ=0
    g33: LineSegment StartX=9.15 StartY=-31.3546 StartZ=0 EndX=9.15 EndY=-34.6454 EndZ=0
    g34: Circle [constr] CenterX=12 CenterY=-33 CenterZ=0 NormalX=0 NormalY=0 NormalZ=1 AngleXU=0 Radius=3.2909
    g35: LineSegment StartX=-21.65 StartY=15.5546 StartZ=0 EndX=-18.8 EndY=13.9091 EndZ=0
    g36: LineSegment StartX=-18.8 StartY=13.9091 StartZ=0 EndX=-15.95 EndY=15.5546 EndZ=0
    g37: LineSegment StartX=-15.95 StartY=15.5546 StartZ=0 EndX=-15.95 EndY=18.8454 EndZ=0
    g38: LineSegment StartX=-15.95 StartY=18.8454 StartZ=0 EndX=-18.8 EndY=20.4909 EndZ=0
    g39: LineSegment StartX=-18.8 StartY=20.4909 StartZ=0 EndX=-21.65 EndY=18.8454 EndZ=0
    g40: LineSegment StartX=-21.65 StartY=18.8454 StartZ=0 EndX=-21.65 EndY=15.5546 EndZ=0
    g41: Circle [constr] CenterX=-18.8 CenterY=17.2 CenterZ=0 NormalX=0 NormalY=0 NormalZ=1 AngleXU=0 Radius=3.2909
  constraints (96):
    c: Coincident(g0,g1)
    c: Coincident(g1,g2)
    c: Coincident(g2,g3)
    c: Coincident(g3,g4)
    c: Coincident(g4,g5)
    c: Coincident(g5,g0)
    c: Equal(g0, g1-g5) x5
    c: PointOnObject(g0,g6)
    c: PointOnObject(g1,g6)
    c: PointOnObject(g2,g6)
    c: PointOnObject(g3,g6)
    c: PointOnObject(g4,g6)
    c: PointOnObject(g5,g6)
    c: Coincident(g6,g-5)
    c: Coincident(g7,g8)
    c: Coincident(g8,g9)
    c: Coincident(g9,g10)
    c: Coincident(g10,g11)
    c: Coincident(g11,g12)
    c: Coincident(g12,g7)
    c: Equal(g7, g8-g12) x5
    c: PointOnObject(g7,g13)
    c: PointOnObject(g8,g13)
    c: PointOnObject(g9,g13)
    c: PointOnObject(g10,g13)
    c: PointOnObject(g11,g13)
    c: PointOnObject(g12,g13)
    c: Coincident(g13,g-6)
    c: Coincident(g14,g15)
    c: Coincident(g15,g16)
    c: Coincident(g16,g17)
    c: Coincident(g17,g18)
    c: Coincident(g18,g19)
    c: Coincident(g19,g14)
    c: Equal(g14, g15-g19) x5
    c: PointOnObject(g14,g20)
    c: PointOnObject(g15,g20)
    c: PointOnObject(g16,g20)
    c: PointOnObject(g17,g20)
    c: PointOnObject(g18,g20)
    c: PointOnObject(g19,g20)
    c: Coincident(g20,g-4)
    c: Coincident(g21,g22)
    c: Coincident(g22,g23)
    c: Coincident(g23,g24)
    c: Coincident(g24,g25)
    c: Coincident(g25,g26)
    c: Coincident(g26,g21)
    c: Equal(g21, g22-g26) x5
    c: PointOnObject(g21,g27)
    c: PointOnObject(g22,g27)
    c: PointOnObject(g23,g27)
    c: PointOnObject(g24,g27)
    c: PointOnObject(g25,g27)
    c: PointOnObject(g26,g27)
    c: Coincident(g27,g-7)
    c: Coincident(g28,g29)
    c: Coincident(g29,g30)
    c: Coincident(g30,g31)
    c: Coincident(g31,g32)
    c: Coincident(g32,g33)
    c: Coincident(g33,g28)
    c: Equal(g28, g29-g33) x5
    c: PointOnObject(g28,g34)
    c: PointOnObject(g29,g34)
    c: PointOnObject(g30,g34)
    c: PointOnObject(g31,g34)
    c: PointOnObject(g32,g34)
    c: PointOnObject(g33,g34)
    c: Coincident(g34,g-3)
    c: DistanceX(g0,g1) = 5.7
    c: Equal(g3,g11)
    c: Vertical(g5)
    c: Vertical(g12)
    c: Vertical(g18)
    c: Vertical(g26)
    c: Vertical(g33)
    c: DistanceX(g25,g23) = 5.7
    c: Equal(g24,g31)
    c: Equal(g24,g16)
    c: Coincident(g35,g36)
    c: Coincident(g36,g37)
    c: Coincident(g37,g38)
    c: Coincident(g38,g39)
    c: Coincident(g39,g40)
    c: Coincident(g40,g35)
    c: Equal(g35, g36-g40) x5
    c: PointOnObject(g35,g41)
    c: PointOnObject(g36,g41)
    c: PointOnObject(g37,g41)
    c: PointOnObject(g38,g41)
    c: PointOnObject(g39,g41)
    c: PointOnObject(g40,g41)
    c: Coincident(g41,g-8)
    c: Vertical(g37)
    c: DistanceX(g39,g37) = 5.7
FEATURE [PartDesign::Pocket] Pocket014  label="Hex Inserts"
  BaseFeature = -> Pocket013
  Direction = (0,1,0)
  Length = 2.63
  Length2 = 5
  Placement = pos=(0,0,0) rot=(0,-1,0;1.5708rad)
  Profile = -> Sketch026
  ReferenceAxis = -> Sketch026 [N_Axis]
  Refine = true
  Suppressed = false
  Type = 0
  expr: Length = <<Dimensions>>.M3HexD
FEATURE [PartDesign::Pad] Pad004  label="Hex Inserts Support"
  BaseFeature = -> Pocket014
  Direction = (0,1,0)
  Length = 0.4
  Length2 = 10
  Placement = pos=(0,0,0) rot=(0,-1,0;1.5708rad)
  Profile = -> Pocket014 [Edge143,Edge147,Edge153,Edge155,Edge145]
  Refine = true
  Suppressed = false
  Type = 0
FEATURE [PartDesign::SubShapeBinder] Binder008
  BindCopyOnChange = 0
  BindMode = 0
  ClaimChildren = false
  Context = -> Part004 [Body005.Binder008.]
  Fuse = false
  MakeFace = true
  OffsetFill = false
  OffsetIntersection = false
  OffsetJoinType = 0
  OffsetOpenResult = false
  PartialLoad = false
  Refine = true
  Relative = true
  Support = -> [Sketch014]
  _Version = 2
FEATURE [Sketcher::SketchObject] Sketch027
  ArcFitTolerance = 1e-06
  AttachmentSupport = -> [XZ_Plane025]
  ExternalGeometry = -> [Binder008]
  FullyConstrained = true
  MakeInternals = false
  MapMode = 5
  Placement = pos=(0,0,0) rot=(0,0.707107,0.707107;3.14159rad)
  sketch-geometry (4):
    g0: LineSegment StartX=-23.1 StartY=39.5 StartZ=0 EndX=-23.1 EndY=-21.5 EndZ=0
    g1: LineSegment StartX=-23.1 StartY=-21.5 StartZ=0 EndX=18.5 EndY=-21.5 EndZ=0
    g2: LineSegment StartX=18.5 StartY=-21.5 StartZ=0 EndX=18.5 EndY=39.5 EndZ=0
    g3: LineSegment StartX=18.5 StartY=39.5 StartZ=0 EndX=-23.1 EndY=39.5 EndZ=0
  constraints (12):
    c: Vertical(g0)
    c: Coincident(g0,g1)
    c: Horizontal(g1)
    c: Coincident(g1,g2)
    c: Vertical(g2)
    c: Coincident(g2,g3)
    c: Horizontal(g3)
    c: DistanceX(g-3,g2) = 6.5
    c: DistanceY(g-3,g2) = 6.5
    c: DistanceY(g1,g-4) = 6.5
    c: Coincident(g0,g3)
    c: DistanceX(g0,g-6) = 6.5
FEATURE [PartDesign::Pad] Pad006
  Direction = (0,1,-2e-16)
  Length = 6
  Length2 = 10
  Placement = pos=(0,0,0) rot=(1,0,0;1.5708rad)
  Profile = -> Sketch027
  ReferenceAxis = -> Sketch027 [N_Axis]
  Refine = true
  Suppressed = false
  Type = 0
FEATURE [PartDesign::Fillet] Fillet008  label="Large Corner Fillet"
  Base = -> Pad004 [Edge136]
  BaseFeature = -> Pad004
  Placement = pos=(0,0,0) rot=(0,-1,0;1.5708rad)
  Radius = 6
  Refine = true
  SupportTransform = false
  Suppressed = false
  UseAllEdges = false
FEATURE [PartDesign::Fillet] Fillet009  label="Sharp Corner Fillet"
  Base = -> Fillet008 [Edge51]
  BaseFeature = -> Fillet008
  Placement = pos=(0,0,0) rot=(0,-1,0;1.5708rad)
  Radius = 1
  Refine = true
  SupportTransform = false
  Suppressed = false
  UseAllEdges = false
FEATURE [PartDesign::FeatureBase] Clone
  BaseFeature = -> Body001
  Suppressed = false
FEATURE [PartDesign::Body] Body006  label="TensionerGearBody"
  AllowCompound = false
  Group = -> [Clone]
  Origin = -> Origin026
  Placement = pos=(12.5,0,0) rot=(0,0,1;0rad)
  Tip = -> Clone
FEATURE [App::Part] Part002  label="Drive Gear"
  Group = -> [Body001,Body006]
  Origin = -> Origin018
FEATURE [PartDesign::Fillet] Fillet016  label="Axle Corner Fillet"
  Base = -> Fillet009 [Edge55]
  BaseFeature = -> Fillet009
  Placement = pos=(0,0,0) rot=(0,-1,0;1.5708rad)
  Radius = 4
  Refine = true
  SupportTransform = false
  Suppressed = false
  UseAllEdges = false
FEATURE [PartDesign::Chamfer] Chamfer009  label="Edge Chamfer"
  Angle = 45
  Base = -> Fillet016 [Edge57,Edge64,Edge61,Edge66]
  BaseFeature = -> Fillet016
  ChamferType = 0
  FlipDirection = false
  Placement = pos=(0,0,0) rot=(0,-1,0;1.5708rad)
  Refine = true
  Size = 1
  Size2 = 1
  SupportTransform = false
  Suppressed = false
  UseAllEdges = false
FEATURE [Sketcher::SketchObject] Sketch030
  ArcFitTolerance = 1e-06
  AttachmentSupport = -> [Chamfer009]
  ExternalGeometry = -> [Chamfer009]
  FullyConstrained = true
  MakeInternals = false
  MapMode = 5
  Placement = pos=(0,0,0) rot=(0.57735,-0.57735,-0.57735;4.18879rad)
  sketch-geometry (4):
    g0: ArcOfCircle CenterX=-44 CenterY=6.7e-15 CenterZ=0 NormalX=0 NormalY=0 NormalZ=1 AngleXU=0 Radius=11.2 StartAngle=1.5708 EndAngle=4.71239
    g1: ArcOfCircle CenterX=-40 CenterY=7.5e-15 CenterZ=0 NormalX=0 NormalY=0 NormalZ=1 AngleXU=0 Radius=11.2 StartAngle=4.71239 EndAngle=7.85398
    g2: LineSegment StartX=-44 StartY=11.2 StartZ=0 EndX=-40 EndY=11.2 EndZ=0
    g3: LineSegment StartX=-44 StartY=-11.2 StartZ=0 EndX=-40 EndY=-11.2 EndZ=0
  constraints (9):
    c: Tangent(g0,g2) = 1.5708
    c: Tangent(g0,g3) = -1.5708
    c: Tangent(g1,g2) = 1.5708
    c: Tangent(g1,g3) = -1.5708
    c: Equal(g0,g1)
    c: Horizontal(g3)
    c: Diameter(g1) = 22.4
    c: Coincident(g0,g-3)
    c: DistanceX(g3,g3) = 4
FEATURE [PartDesign::Pocket] Pocket017
  BaseFeature = -> Chamfer009
  Direction = (0,-1,0)
  Length = 2.2
  Length2 = 5
  Placement = pos=(0,0,0) rot=(0,-1,0;1.5708rad)
  Profile = -> Sketch030
  ReferenceAxis = -> Sketch030 [N_Axis]
  Refine = true
  Suppressed = false
  Type = 0
FEATURE [PartDesign::SubShapeBinder] Binder009  label="Body Screw Binders"
  BindCopyOnChange = 0
  BindMode = 0
  ClaimChildren = false
  Context = -> Part005 [Body007.Binder009.]
  Fuse = false
  MakeFace = true
  OffsetFill = false
  OffsetIntersection = false
  OffsetJoinType = 0
  OffsetOpenResult = false
  PartialLoad = false
  Refine = true
  Relative = true
  Support = -> [Sketch014]
  _Version = 2
FEATURE [Sketcher::SketchObject] Sketch036  label="BaseSketch"
  ArcFitTolerance = 1e-06
  AttachmentOffset = pos=(0,0,-22) rot=(0,0,1;0rad)
  AttachmentSupport = -> [XZ_Plane028]
  ExternalGeometry = -> [Binder009]
  FullyConstrained = true
  MakeInternals = false
  MapMode = 5
  Placement = pos=(0,22,-4.9e-15) rot=(1,0,0;1.5708rad)
  sketch-geometry (22):
    g0: LineSegment StartX=-18.5 StartY=39.5 StartZ=0 EndX=-18.5 EndY=-21.5 EndZ=0
    g1: LineSegment [constr] StartX=-18.5 StartY=-21.5 StartZ=0 EndX=14 EndY=-21.5 EndZ=0
    g2: LineSegment StartX=14 StartY=-21.5 StartZ=0 EndX=14 EndY=-12.5 EndZ=0
    g3: ArcOfCircle CenterX=0 CenterY=0 CenterZ=0 NormalX=0 NormalY=0 NormalZ=1 AngleXU=0 Radius=6.5 StartAngle=0.720958 EndAngle=5.56223
    g4: Circle CenterX=-3 CenterY=15 CenterZ=0 NormalX=0 NormalY=0 NormalZ=1 AngleXU=0 Radius=1.7
    g5: Circle CenterX=-3 CenterY=-15 CenterZ=0 NormalX=0 NormalY=0 NormalZ=1 AngleXU=0 Radius=1.7
    g6: LineSegment [constr] StartX=4.88263 StartY=4.29068 StartZ=0 EndX=14 EndY=12.5 EndZ=0
    g7: LineSegment StartX=4.88263 StartY=-4.29068 StartZ=0 EndX=14 EndY=-12.5 EndZ=0
    g8: LineSegment [constr] StartX=14 StartY=12.5 StartZ=0 EndX=14 EndY=-12.5 EndZ=0
    g9: LineSegment [constr] StartX=4.88263 StartY=4.29068 StartZ=0 EndX=4.88263 EndY=-4.29068 EndZ=0
    g10: LineSegment StartX=23.1 StartY=39.5 StartZ=0 EndX=-18.5 EndY=39.5 EndZ=0
    g11: LineSegment StartX=4.88263 StartY=26.5 StartZ=0 EndX=23.1 EndY=26.5 EndZ=0
    g12: LineSegment StartX=23.1 StartY=26.5 StartZ=0 EndX=23.1 EndY=39.5 EndZ=0
    g13: LineSegment StartX=4.88263 StartY=26.5 StartZ=0 EndX=4.88263 EndY=4.29068 EndZ=0
    g14: Circle CenterX=16.6 CenterY=33 CenterZ=0 NormalX=0 NormalY=0 NormalZ=1 AngleXU=0 Radius=1.7
    g15: Circle CenterX=-12 CenterY=33 CenterZ=0 NormalX=0 NormalY=0 NormalZ=1 AngleXU=0 Radius=1.7
    g16: Circle CenterX=-12 CenterY=-15 CenterZ=0 NormalX=0 NormalY=0 NormalZ=1 AngleXU=0 Radius=1.7
    g17: LineSegment StartX=-18.5 StartY=-21.5 StartZ=0 EndX=-23.75 EndY=-21.5 EndZ=0
    g18: LineSegment StartX=-23.75 StartY=-21.5 StartZ=0 EndX=-23.75 EndY=-31.3 EndZ=0
    g19: LineSegment StartX=-23.75 StartY=-31.3 StartZ=0 EndX=36.25 EndY=-31.3 EndZ=0
    g20: LineSegment StartX=36.25 StartY=-31.3 StartZ=0 EndX=36.25 EndY=-21.5 EndZ=0
    g21: LineSegment StartX=36.25 StartY=-21.5 StartZ=0 EndX=14 EndY=-21.5 EndZ=0
  constraints (58):
    c: Coincident(g0,g1)
    c: Coincident(g1,g2)
    c: Coincident(g10,g0)
    c: Vertical(g0)
    c: Vertical(g2)
    c: Horizontal(g1)
    c: DistanceX(g0,g-3) = 6.5
    c: DistanceY(g0,g-4) = 6.5
    c: Coincident(g3,g-1)
    c: Diameter(g3) = 13
    c: DistanceY(g-3,g0) = 6.5
    c: Coincident(g4,g-5)
    c: Equal(g4,g-5)
    c: Coincident(g5,g-6)
    c: Equal(g5,g-6)
    c: DistanceY(g7,g6) = 25
    c: Symmetric(g6,g7,g-1)
    c: PointOnObject(g2,g7)
    c: Coincident(g8,g6)
    c: Coincident(g8,g2)
    c: Vertical(g8)
    c: Coincident(g7,g3)
    c: Coincident(g6,g3)
    c: Angle(g7,g6) = 1.46608
    c: Coincident(g9,g3)
    c: Coincident(g9,g3)
    c: Vertical(g9)
    c: Horizontal(g10)
    c: Horizontal(g11)
    c: Coincident(g12,g11)
    c: Vertical(g12)
    c: DistanceX(g3,g1) = 14
    c: Coincident(g13,g11)
    c: Vertical(g13)
    c: DistanceX(g-7,g12) = 6.5
    c: Coincident(g10,g12)
    c: DistanceY(g11,g-7) = 6.5
    c: Coincident(g13,g3)
    c: Coincident(g14,g-7)
    c: Equal(g14,g-7)
    c: Coincident(g15,g-3)
    c: Equal(g15,g-3)
    c: Coincident(g16,g-4)
    c: Equal(g16,g-4)
    c: Coincident(g0,g17)
    c: Horizontal(g17)
    c: Coincident(g17,g18)
    c: Vertical(g18)
    c: Coincident(g18,g19)
    c: Horizontal(g19)
    c: Coincident(g19,g20)
    c: Vertical(g20)
    c: Coincident(g20,g21)
    c: Coincident(g21,g1)
    c: Horizontal(g21)
    c: DistanceX(g19,g19) = 60
    c: DistanceY(g20,g20) = 9.8
    c: DistanceX(g17,g0) = 5.25
FEATURE [PartDesign::Pad] Pad008  label="Body Pad"
  Direction = (0,-1,2e-16)
  Length = 12.5
  Length2 = 10
  Placement = pos=(0,0,0) rot=(1,0,0;1.5708rad)
  Profile = -> Sketch036
  ReferenceAxis = -> Sketch036 [N_Axis]
  Refine = true
  Suppressed = false
  Type = 0
FEATURE [PartDesign::Fillet] Fillet021
  Base = -> Pad008 [Edge8]
  BaseFeature = -> Pad008
  Placement = pos=(0,0,0) rot=(1,0,0;1.5708rad)
  Radius = 6.5
  Refine = true
  SupportTransform = false
  Suppressed = false
  UseAllEdges = false
FEATURE [PartDesign::Fillet] Fillet022
  Base = -> Fillet021 [Edge50,Edge44]
  BaseFeature = -> Fillet021
  Placement = pos=(0,0,0) rot=(1,0,0;1.5708rad)
  Radius = 2
  Refine = true
  SupportTransform = false
  Suppressed = false
  UseAllEdges = false
FEATURE [PartDesign::SubShapeBinder] Binder010  label="Filament Path Binder"
  BindCopyOnChange = 0
  BindMode = 0
  ClaimChildren = false
  Context = -> Part005 [Body007.Binder010.]
  Fuse = false
  MakeFace = true
  OffsetFill = false
  OffsetIntersection = false
  OffsetJoinType = 0
  OffsetOpenResult = false
  PartialLoad = false
  Refine = true
  Relative = true
  Support = -> [Sketch006]
  _Version = 2
FEATURE [App::DocumentObjectGroup] Group002  label="Base Sketches"
  Group = -> [Sketch006,Sketch014,Sketch]
FEATURE [Sketcher::SketchObject] Sketch037
  ArcFitTolerance = 1e-06
  AttachmentSupport = -> [Pad008]
  ExternalGeometry = -> [Binder010]
  FullyConstrained = true
  MakeInternals = false
  MapMode = 5
  Placement = pos=(0,1.74e-14,39.5) rot=(0,0,1;3.14159rad)
  sketch-geometry (1):
    g0: Circle CenterX=-6.25 CenterY=-15.85 CenterZ=0 NormalX=0 NormalY=0 NormalZ=1 AngleXU=0 Radius=1.425
  constraints (2):
    c: Coincident(g0,g-3)
    c: Equal(g0,g-3)
FEATURE [Sketcher::SketchObject] Sketch038  label="Tensioner Latch Sketch"
  ArcFitTolerance = 1e-06
  FullyConstrained = true
  MakeInternals = false
  MapMode = 5
  Placement = pos=(23.1,0,0) rot=(0.707107,0,0.707107;3.14159rad)
  sketch-geometry (8):
    g0: LineSegment StartX=19.15 StartY=-9.7 StartZ=0 EndX=28.85 EndY=-9.7 EndZ=0
    g1: LineSegment StartX=28.85 StartY=-9.7 StartZ=0 EndX=28.85 EndY=0 EndZ=0
    g2: LineSegment StartX=28.85 StartY=0 StartZ=0 EndX=19.15 EndY=0 EndZ=0
    g3: LineSegment StartX=19.15 StartY=0 StartZ=0 EndX=19.15 EndY=-9.7 EndZ=0
    g4: Circle CenterX=24 CenterY=-4.85 CenterZ=0 NormalX=0 NormalY=0 NormalZ=1 AngleXU=0 Radius=2.75
    g5: LineSegment [constr] StartX=19.15 StartY=0 StartZ=0 EndX=28.85 EndY=-9.7 EndZ=0
    g6: LineSegment [constr] StartX=24 StartY=-9.7 StartZ=0 EndX=24 EndY=0 EndZ=0
    g7: LineSegment [constr] StartX=0 StartY=0 StartZ=0 EndX=19.15 EndY=0 EndZ=0
  constraints (20):
    c: Coincident(g0,g1)
    c: Coincident(g1,g2)
    c: Coincident(g2,g3)
    c: Coincident(g3,g0)
    c: Horizontal(g0)
    c: Horizontal(g2)
    c: Vertical(g1)
    c: Vertical(g3)
    c: Diameter(g4) = 5.5
    c: Coincident(g5,g2)
    c: Coincident(g5,g0)
    c: DistanceY(g1,g1) = 9.7
    c: Symmetric(g5,g5,g4)
    c: Equal(g2,g1)
    c: Symmetric(g0,g0,g6)
    c: Symmetric(g2,g2,g6)
    c: DistanceX(g-1,g6) = 24
    c: Coincident(g7,g-1)
    c: Coincident(g7,g2)
    c: Horizontal(g7)
FEATURE [PartDesign::Pocket] Pocket018  label="Tensioner Latch Cutout"
  BaseFeature = -> Fillet022
  Direction = (-1,1e-16,2e-16)
  Length = 0
  Length2 = 5
  Placement = pos=(0,0,0) rot=(1,0,0;1.5708rad)
  Profile = -> Sketch038
  ReferenceAxis = -> Sketch038 [N_Axis]
  Refine = true
  Suppressed = false
  Type = 3
  UpToFace = -> Fillet022 [Face10]
FEATURE [PartDesign::Pocket] Pocket019
  BaseFeature = -> Pocket018
  Direction = (0,1,0)
  Length = 0.2
  Length2 = 5
  Placement = pos=(0,0,0) rot=(1,0,0;1.5708rad)
  Profile = -> Pocket018 [Face24]
  Refine = true
  Suppressed = false
  Type = 0
FEATURE [PartDesign::Pad] Pad009
  BaseFeature = -> Pocket019
  Direction = (0,-1,0)
  Length = 9.5
  Length2 = 10
  Placement = pos=(0,0,0) rot=(1,0,0;1.5708rad)
  Profile = -> Pocket019 [Face23]
  Refine = true
  Suppressed = false
  Type = 0
FEATURE [Sketcher::SketchObject] Sketch039
  ArcFitTolerance = 1e-06
  AttachmentSupport = -> [Pad009]
  FullyConstrained = true
  MakeInternals = false
  MapMode = 5
  Placement = pos=(0,1.07e-14,0) rot=(1,0,0;1.5708rad)
  sketch-geometry (1):
    g0: Circle CenterX=0 CenterY=0 CenterZ=0 NormalX=0 NormalY=0 NormalZ=1 AngleXU=0 Radius=8
  constraints (2):
    c: Coincident(g0,g-1)
    c: Diameter(g0) = 16
FEATURE [PartDesign::Pocket] Pocket020
  BaseFeature = -> Pad009
  Direction = (0,1,-2e-16)
  Length = 9
  Length2 = 5
  Placement = pos=(0,0,0) rot=(1,0,0;1.5708rad)
  Profile = -> Sketch039
  ReferenceAxis = -> Sketch039 [N_Axis]
  Refine = true
  Suppressed = false
  Type = 0
FEATURE [PartDesign::Fillet] Fillet023
  Base = -> Pocket020 [Edge43,Edge31]
  BaseFeature = -> Pocket020
  Placement = pos=(0,0,0) rot=(1,0,0;1.5708rad)
  Radius = 2
  Refine = true
  SupportTransform = false
  Suppressed = false
  UseAllEdges = false
FEATURE [PartDesign::Fillet] Fillet024
  Base = -> Fillet023 [Edge46,Edge8]
  BaseFeature = -> Fillet023
  Placement = pos=(0,0,0) rot=(1,0,0;1.5708rad)
  Radius = 2
  Refine = true
  SupportTransform = false
  Suppressed = false
  UseAllEdges = false
FEATURE [PartDesign::Fillet] Fillet025  label="Sharp edges"
  Base = -> Fillet024 [Edge7,Edge72,Edge59,Edge73]
  BaseFeature = -> Fillet024
  Placement = pos=(0,0,0) rot=(1,0,0;1.5708rad)
  Radius = 1
  Refine = true
  SupportTransform = false
  Suppressed = false
  UseAllEdges = false
FEATURE [PartDesign::Fillet] Fillet026  label="tensioner clearance fillet"
  Base = -> Pocket007 [Edge26,Edge30]
  BaseFeature = -> Pocket007
  Placement = pos=(0,0,0) rot=(1,0,0;1.5708rad)
  Radius = 2
  Refine = true
  SupportTransform = false
  Suppressed = false
  UseAllEdges = false
FEATURE [PartDesign::Fillet] Fillet027  label="gear trunk fillet"
  Base = -> Fillet026 [Edge47,Edge18,Edge79,Edge64]
  BaseFeature = -> Fillet026
  Placement = pos=(0,0,0) rot=(1,0,0;1.5708rad)
  Radius = 2
  Refine = true
  SupportTransform = false
  Suppressed = false
  UseAllEdges = false
FEATURE [PartDesign::Fillet] Fillet028  label="axle tabs fillet"
  Base = -> Fillet027 [Edge91,Edge89,Edge4,Edge9]
  BaseFeature = -> Fillet027
  Placement = pos=(0,0,0) rot=(1,0,0;1.5708rad)
  Radius = 2
  Refine = true
  SupportTransform = false
  Suppressed = false
  UseAllEdges = false
FEATURE [PartDesign::SubShapeBinder] Binder011  label="holes binder"
  BindCopyOnChange = 0
  BindMode = 0
  ClaimChildren = false
  Context = -> Part006 [Body008.Binder011.]
  Fuse = false
  MakeFace = true
  OffsetFill = false
  OffsetIntersection = false
  OffsetJoinType = 0
  OffsetOpenResult = false
  PartialLoad = false
  Refine = true
  Relative = true
  Support = -> [Sketch014]
  _Version = 2
FEATURE [Sketcher::SketchObject] Sketch040  label="Latch Base Sketch"
  ArcFitTolerance = 1e-06
  AttachmentSupport = -> [XZ_Plane030]
  ExternalGeometry = -> [Binder011]
  FullyConstrained = false
  MakeInternals = false
  MapMode = 5
  Placement = pos=(0,0,0) rot=(1,0,0;1.5708rad)
  sketch-geometry (25):
    g0: LineSegment StartX=-18.1 StartY=39.4 StartZ=0 EndX=-18.1 EndY=21.0678 EndZ=0
    g1: LineSegment StartX=23.5 StartY=39.4 StartZ=0 EndX=-18.1 EndY=39.4 EndZ=0
    g2: Circle [constr] CenterX=-11.6 CenterY=32.9 CenterZ=0 NormalX=0 NormalY=0 NormalZ=1 AngleXU=0 Radius=13.5
    g3: LineSegment StartX=-18.1 StartY=21.0678 StartZ=0 EndX=-11.6 EndY=21.0678 EndZ=0
    g4: LineSegment StartX=-11.6 StartY=21.0678 StartZ=0 EndX=-11.6 EndY=32.9 EndZ=0
    g5: LineSegment [constr] StartX=-11.6 StartY=32.9 StartZ=0 EndX=-18.1 EndY=21.0678 EndZ=0
    g6: LineSegment StartX=19 StartY=26.4 StartZ=0 EndX=23.5 EndY=26.4 EndZ=0
    g7: Circle [constr] CenterX=-11.6 CenterY=32.9 CenterZ=0 NormalX=0 NormalY=0 NormalZ=1 AngleXU=0 Radius=30.3
    g8: LineSegment StartX=23.5 StartY=26.4 StartZ=0 EndX=23.5 EndY=32.9 EndZ=0
    g9: LineSegment StartX=33.5 StartY=42.4992 StartZ=0 EndX=23.5 EndY=39.4 EndZ=0
    g10: LineSegment StartX=23.5 StartY=32.9 StartZ=0 EndX=33.4819 EndY=39.8062 EndZ=0
    g11: LineSegment StartX=33.4819 StartY=39.8062 StartZ=0 EndX=33.5 EndY=42.4992 EndZ=0
    g12: Circle [constr] CenterX=-11.6 CenterY=32.9 CenterZ=0 NormalX=0 NormalY=0 NormalZ=1 AngleXU=0 Radius=11.8322
    g13: LineSegment StartX=-11.6 StartY=32.9 StartZ=0 EndX=-0.464471 EndY=32.9 EndZ=0
    g14: LineSegment [constr] StartX=-0.464471 StartY=32.9 StartZ=0 EndX=17 EndY=32.9 EndZ=0
    g15: LineSegment StartX=-0.464471 StartY=32.9 StartZ=0 EndX=-0.464471 EndY=28.9 EndZ=0
    g16: LineSegment StartX=-0.464471 StartY=28.9 StartZ=0 EndX=2.53553 EndY=28.9 EndZ=0
    g17: LineSegment StartX=2.53553 StartY=28.9 StartZ=0 EndX=5.08332 EndY=35.9 EndZ=0
    g18: LineSegment StartX=5.08332 StartY=35.9 StartZ=0 EndX=19 EndY=35.9 EndZ=0
    g19: LineSegment StartX=19 StartY=35.9 StartZ=0 EndX=19 EndY=31.2 EndZ=0
    g20: LineSegment StartX=17 StartY=31.2 StartZ=0 EndX=19 EndY=31.2 EndZ=0
    g21: LineSegment [constr] StartX=23.5 StartY=39.4 StartZ=0 EndX=23.5 EndY=32.9 EndZ=0
    g22: LineSegment StartX=17 StartY=31.2 StartZ=0 EndX=17 EndY=28.4 EndZ=0
    g23: LineSegment StartX=17 StartY=28.4 StartZ=0 EndX=19 EndY=26.4 EndZ=0
    g24: LineSegment [constr] StartX=19 StartY=31.2 StartZ=0 EndX=19 EndY=26.4 EndZ=0
  constraints (62):
    c: Coincident(g0,g3)
    c: Coincident(g6,g8)
    c: Coincident(g9,g1)
    c: Coincident(g1,g0)
    c: Vertical(g0)
    c: Horizontal(g1)
    c: DistanceY(g-3,g0) = 6.5
    c: DistanceX(g-4,g9) = 6.5
    c: Coincident(g2,g-3)
    c: Diameter(g2) = 27
    c: Coincident(g3,g4)
    c: Horizontal(g3)
    c: Coincident(g4,g13)
    c: DistanceX(g0,g2) = 6.5
    c: Coincident(g5,g2)
    c: Coincident(g5,g0)
    c: Distance(g5,g5) = 13.5
    c: DistanceY(g8,g-4) = 6.5
    c: Coincident(g23,g6)
    c: Horizontal(g6)
    c: Coincident(g4,g2)
    c: Coincident(g14,g-4)
    c: Coincident(g7,g2)
    c: Tangent(g7,g-4)
    c: Coincident(g8,g10)
    c: Vertical(g8)
    c: Coincident(g11,g9)
    c: Coincident(g10,g11)
    c: Coincident(g12,g2)
    c: Tangent(g3,g12) = -1.5708
    c: Coincident(g13,g14)
    c: Coincident(g13,g15)
    c: PointOnObject(g15,g12)
    c: Coincident(g15,g16)
    c: Horizontal(g16)
    c: Coincident(g16,g17)
    c: Coincident(g17,g18)
    c: Horizontal(g18)
    c: DistanceY(g15,g13) = 4
    c: DistanceX(g16,g16) = 3
    c: Coincident(g18,g19)
    c: Vertical(g19)
    c: Coincident(g20,g19)
    c: Coincident(g21,g1)
    c: Coincident(g21,g8)
    c: Horizontal(g20)
    c: Coincident(g22,g23)
    c: Vertical(g22)
    c: Coincident(g20,g22)
    c: DistanceX(g14,g18) = 2
    c: DistanceX(g20,g20) = 2
    c: Angle(g17,g18) = 1.91986
    c: Horizontal(g14)
    c: Vertical(g15)
    c: DistanceY(g18,g1) = 3.5
    c: DistanceY(g19,g19) = 4.7
    c: Coincident(g24,g19)
    c: Coincident(g24,g6)
    c: Vertical(g24)
    c: Angle(g24,g23) = 0.785398
    c: DistanceX(g1,g9) = 10
    c: Symmetric(g1,g6,g8)
FEATURE [PartDesign::Pad] Pad010
  Direction = (0,-1,2e-16)
  Length = 9
  Length2 = 10
  Placement = pos=(0,0,0) rot=(1,0,0;1.5708rad)
  Profile = -> Sketch040
  ReferenceAxis = -> Sketch040 [N_Axis]
  Refine = true
  Reversed = true
  Suppressed = false
  Type = 0
FEATURE [PartDesign::Fillet] Fillet029  label="Large Corner"
  Base = -> Pad010 [Edge23]
  BaseFeature = -> Pad010
  Placement = pos=(0,0,0) rot=(1,0,0;1.5708rad)
  Radius = 6.5
  Refine = true
  SupportTransform = false
  Suppressed = false
  UseAllEdges = false
FEATURE [App::Link] Extruder_BodyLower  label="Extruder-BodyLower001"
  LinkPlacement = pos=(-15.1847,-103.447,40.2497) rot=(0,0,1;0rad)
  LinkedObject = -> Part005
  Placement = pos=(-15.1847,-103.447,40.2497) rot=(0,0,1;0rad)
FEATURE [App::FeaturePython] GroundedJoint  # Assembly grounded joint (typed FeaturePython)
  ObjectToGround = -> Extruder_BodyLower
  Placement = pos=(-15.1847,-103.447,40.2497) rot=(0,0,1;0rad)
FEATURE [App::Link] Tensioner_Latch  label="Tensioner-Latch001"
  LinkPlacement = pos=(-47.2204,-111.366,56.3319) rot=(0.7045,0.085786,0.7045;3.31275rad)
  LinkedObject = -> Part006
  Placement = pos=(-47.2204,-111.366,56.3319) rot=(0.7045,0.085786,0.7045;3.31275rad)
FEATURE [App::Link] Tensioner  label="Tensioner001"
  LinkPlacement = pos=(-4.06374,-84.7417,34.5497) rot=(0.582122,0.567788,-0.582023;2.10865rad)
  LinkedObject = -> Part003
  Placement = pos=(-4.06374,-84.7417,34.5497) rot=(0.582122,0.567788,-0.582023;2.10865rad)
FEATURE [App::FeaturePython] Joint001  label="Revolute001"  # Assembly joint (typed FeaturePython)
  Activated = true
  AngleMax = 2
  AngleMin = 90
  Detach1 = false
  Detach2 = false
  Distance = 0
  Distance2 = 0
  EnableAngleMax = false
  EnableAngleMin = true
  EnableLengthMax = false
  EnableLengthMin = false
  JointType = 1 (Revolute)
  LengthMax = 0
  LengthMin = 0
  Offset1 = pos=(-35.3,13.9,0) rot=(0,0,1;0rad)
  Placement1 = pos=(11.55,35.9,-24.5) rot=(0,1,0;3.14159rad)
  Placement2 = pos=(18.8,-3.6e-15,-17.2) rot=(1,0,0;1.5708rad)
  Reference1 = -> Assembly [Extruder_BodyLower.Body007.Binder009.Edge7,Extruder_BodyLower.Body007.Binder009.Vertex2]
  Reference2 = -> Assembly [Tensioner.Body003.Edge14,Tensioner.Body003.Edge14]
FEATURE [Sketcher::SketchObject] Sketch042
  ArcFitTolerance = 1e-06
  AttachmentSupport = -> [XZ_Plane033]
  FullyConstrained = false
  MakeInternals = false
  MapMode = 5
  Placement = pos=(0,0,0) rot=(1,0,0;1.5708rad)
  sketch-geometry (8):
    g0: LineSegment StartX=-11.6782 StartY=19.6096 StartZ=0 EndX=14.1697 EndY=19.6096 EndZ=0
    g1: LineSegment StartX=14.1697 StartY=19.6096 StartZ=0 EndX=14.1697 EndY=28.5688 EndZ=0
    g2: LineSegment StartX=-11.6782 StartY=32.7888 StartZ=0 EndX=-11.6782 EndY=19.6096 EndZ=0
    g3: LineSegment StartX=-2.60034 StartY=32.7888 StartZ=0 EndX=-11.6782 EndY=32.7888 EndZ=0
    g4: LineSegment StartX=14.1697 StartY=28.5688 StartZ=0 EndX=0.426484 EndY=28.5688 EndZ=0
    g5: ArcOfCircle CenterX=0.426484 CenterY=29.8688 CenterZ=0 NormalX=0 NormalY=0 NormalZ=1 AngleXU=0 Radius=1.3 StartAngle=3.15779 EndAngle=4.71239
    g6: GeomPoint [constr] X=-0.880539 Y=28.5688 Z=0
    g7: ArcOfCircle CenterX=-4.33667 CenterY=29.7916 CenterZ=0 NormalX=0 NormalY=0 NormalZ=1 AngleXU=0 Radius=3.46378 StartAngle=0.0161965 EndAngle=1.04572
  constraints (16):
    c: Coincident(g0,g1)
    c: Coincident(g1,g4)
    c: Coincident(g3,g2)
    c: Coincident(g2,g0)
    c: Horizontal(g0)
    c: Vertical(g1)
    c: Vertical(g2)
    c: Horizontal(g3)
    c: Horizontal(g4)
    c: PointOnObject(g6,g4)
    c: Tangent(g4,g5) = 1.5708
    c: Block(g1)
    c: Radius(g5) = 1.3
    c: Coincident(g3,g7)
    c: Tangent(g5,g7) = 1.5708
    c: DistanceY(g4,g3) = 4.22
FEATURE [PartDesign::Pad] Pad011
  Direction = (0,-1,2e-16)
  Length = 9.5
  Length2 = 10
  Placement = pos=(0,0,0) rot=(1,0,0;1.5708rad)
  Profile = -> Sketch042
  ReferenceAxis = -> Sketch042 [N_Axis]
  Refine = true
  Reversed = true
  Suppressed = false
  Type = 0
FEATURE [App::Link] Tensioner_Shuttle  label="Tensioner Shuttle001"
  LinkPlacement = pos=(-15.1847,-111.947,36.4876) rot=(0.57735,-0.57735,0.57735;2.0944rad)
  LinkedObject = -> Part007
  Placement = pos=(-15.1847,-111.947,36.4876) rot=(0.57735,-0.57735,0.57735;2.0944rad)
FEATURE [App::FeaturePython] Joint  label="Revolute"  # Assembly joint (typed FeaturePython)
  Activated = true
  AngleMax = 179.9
  AngleMin = 90
  Detach1 = false
  Detach2 = false
  Distance = 0
  Distance2 = 0
  EnableAngleMax = false
  EnableAngleMin = false
  EnableLengthMax = false
  EnableLengthMin = false
  JointType = 1 (Revolute)
  LengthMax = 0
  LengthMin = 0
  Offset2 = pos=(0,0,-10) rot=(0,0,1;0rad)
  Placement2 = pos=(-15.6822,7.3e-15,32.9) rot=(0.707107,0,0.707107;3.14159rad)
  Reference1 = -> Assembly [Extruder_BodyLower.Body007.?Edge40,Extruder_BodyLower.Body007.?Edge40]
  Reference2 = -> Assembly [Tensioner_Latch.Body008.Edge21,Tensioner_Latch.Body008.Edge21]
FEATURE [App::FeaturePython] Joint002  label="Slider"  # Assembly joint (typed FeaturePython)
  Activated = true
  AngleMax = 0
  AngleMin = 0
  Detach1 = false
  Detach2 = false
  Distance = 0
  Distance2 = 0
  EnableAngleMax = false
  EnableAngleMin = false
  EnableLengthMax = true
  EnableLengthMin = true
  JointType = 3 (Slider)
  LengthMax = 15.6906
  LengthMin = 0
  Offset1 = pos=(0,-8.5,8.5) rot=(0,0,1;0rad)
  Offset2 = pos=(0,0,0) rot=(0,0,1;1.5708rad)
  Placement1 = pos=(0,-8.5,8.5) rot=(0,0,1;0rad)
  Placement2 = pos=(0,0,0) rot=(0,0,1;1.5708rad)
  Reference1 = -> Assembly [Extruder_BodyLower.Body007.?Face1,Extruder_BodyLower.Body007.?Face1]
  Reference2 = -> Assembly [Tensioner_Shuttle.Body009.?Face10,Tensioner_Shuttle.Body009.?Face10]
FEATURE [Assembly::JointGroup] Joints
  Group = -> [GroundedJoint,Joint,Joint001,Joint002]
FEATURE [Assembly::AssemblyObject] Assembly
  Group = -> [Joints,Extruder_BodyLower,GroundedJoint,Tensioner_Latch,Joint,Tensioner,Joint001,Tensioner_Shuttle,Joint002]
  Origin = -> Origin031
  Type = Assembly
FEATURE [PartDesign::Fillet] Fillet030  label="Large Cam"
  Base = -> Fillet029 [Edge45]
  BaseFeature = -> Fillet029
  Placement = pos=(0,0,0) rot=(1,0,0;1.5708rad)
  Radius = 4
  Refine = true
  SupportTransform = false
  Suppressed = false
  UseAllEdges = false
FEATURE [PartDesign::Fillet] Fillet031  label="Small Cam"
  Base = -> Fillet030 [Edge36]
  BaseFeature = -> Fillet030
  Placement = pos=(0,0,0) rot=(1,0,0;1.5708rad)
  Radius = 1
  Refine = true
  SupportTransform = false
  Suppressed = false
  UseAllEdges = false
FEATURE [PartDesign::Fillet] Fillet032  label="Small Printability"
  Base = -> Fillet031 [Edge23,Edge37,Edge29,Edge57,Edge53,Edge39,Edge41]
  BaseFeature = -> Fillet031
  Placement = pos=(0,0,0) rot=(1,0,0;1.5708rad)
  Radius = 1
  Refine = true
  SupportTransform = false
  Suppressed = false
  UseAllEdges = false
FEATURE [PartDesign::Fillet] Fillet033  label="Large Strain Relief"
  Base = -> Fillet032 [Edge46]
  BaseFeature = -> Fillet032
  Placement = pos=(0,0,0) rot=(1,0,0;1.5708rad)
  Radius = 2
  Refine = true
  SupportTransform = false
  Suppressed = false
  UseAllEdges = false
FEATURE [PartDesign::Fillet] Fillet034  label="Clasp"
  Base = -> Fillet033 [Edge57]
  BaseFeature = -> Fillet033
  Placement = pos=(0,0,0) rot=(1,0,0;1.5708rad)
  Radius = 4
  Refine = true
  SupportTransform = false
  Suppressed = false
  UseAllEdges = false
FEATURE [PartDesign::Fillet] Fillet035
  Base = -> Pad011 [Edge17]
  BaseFeature = -> Pad011
  Placement = pos=(0,0,0) rot=(1,0,0;1.5708rad)
  Radius = 2.5
  Refine = true
  SupportTransform = false
  Suppressed = false
  UseAllEdges = false
FEATURE [Sketcher::SketchObject] Sketch043
  ArcFitTolerance = 1e-06
  AttachmentSupport = -> [Fillet033]
  ExternalGeometry = -> [Binder011]
  FullyConstrained = true
  MakeInternals = false
  MapMode = 5
  Placement = pos=(0,1e-16,0) rot=(1,0,0;1.5708rad)
  sketch-geometry (1):
    g0: Circle CenterX=-11.6 CenterY=32.9 CenterZ=0 NormalX=0 NormalY=0 NormalZ=1 AngleXU=0 Radius=1.7
  constraints (2):
    c: Coincident(g0,g-3)
    c: Equal(g0,g-3)
FEATURE [PartDesign::Pocket] Pocket021
  BaseFeature = -> Fillet034
  Direction = (0,1,-2e-16)
  Length = 9
  Length2 = 5
  Placement = pos=(0,0,0) rot=(1,0,0;1.5708rad)
  Profile = -> Sketch043
  ReferenceAxis = -> Sketch043 [N_Axis]
  Refine = true
  Suppressed = false
  Type = 0
FEATURE [Sketcher::SketchObject] Sketch044
  ArcFitTolerance = 1e-06
  AttachmentSupport = -> [Pad006]
  FullyConstrained = true
  MakeInternals = false
  MapMode = 5
  Placement = pos=(0,2e-15,0) rot=(1,0,0;1.5708rad)
  sketch-geometry (2):
    g0: Circle CenterX=0 CenterY=0 CenterZ=0 NormalX=0 NormalY=0 NormalZ=1 AngleXU=0 Radius=6.65
    g1: Circle CenterX=0 CenterY=0 CenterZ=0 NormalX=0 NormalY=0 NormalZ=1 AngleXU=0 Radius=7.65
  constraints (4):
    c: Diameter(g0) = 13.3
    c: Coincident(g0,g-1)
    c: Diameter(g1) = 15.3
    c: Coincident(g1,g0)
FEATURE [Sketcher::SketchObject] Sketch047
  ArcFitTolerance = 1e-06
  AttachmentSupport = -> [Pad006]
  ExternalGeometry = -> [Pad006]
  FullyConstrained = true
  MakeInternals = false
  MapMode = 5
  Placement = pos=(0,2e-15,0) rot=(1,0,0;1.5708rad)
  sketch-geometry (13):
    g0: LineSegment StartX=-38.5 StartY=47.7 StartZ=0 EndX=-38.5 EndY=27.7 EndZ=0
    g1: LineSegment StartX=-38.5 StartY=27.7 StartZ=0 EndX=43.1 EndY=27.7 EndZ=0
    g2: LineSegment StartX=43.1 StartY=27.7 StartZ=0 EndX=43.1 EndY=47.7 EndZ=0
    g3: LineSegment StartX=-38.5 StartY=47.7 StartZ=0 EndX=-18.5 EndY=47.7 EndZ=0
    g4: LineSegment StartX=43.1 StartY=47.7 StartZ=0 EndX=23.1 EndY=47.7 EndZ=0
    g5: LineSegment [constr] StartX=43.1 StartY=37.7 StartZ=0 EndX=-38.5 EndY=37.7 EndZ=0
    g6: Circle CenterX=33.1 CenterY=37.7 CenterZ=0 NormalX=0 NormalY=0 NormalZ=1 AngleXU=0 Radius=2
    g7: Circle CenterX=-28.5 CenterY=37.7 CenterZ=0 NormalX=0 NormalY=0 NormalZ=1 AngleXU=0 Radius=2
    g8: LineSegment [constr] StartX=-18.5 StartY=47.7 StartZ=0 EndX=23.1 EndY=47.7 EndZ=0
    g9: LineSegment [constr] StartX=2.3 StartY=47.7 StartZ=0 EndX=2.3 EndY=39.5 EndZ=0
    g10: LineSegment StartX=-18.5 StartY=47.7 StartZ=0 EndX=-18.5 EndY=39.5 EndZ=0
    g11: LineSegment StartX=23.1 StartY=47.7 StartZ=0 EndX=23.1 EndY=39.5 EndZ=0
    g12: LineSegment StartX=-18.5 StartY=39.5 StartZ=0 EndX=23.1 EndY=39.5 EndZ=0
  constraints (34):
    c: Coincident(g0,g1)
    c: Coincident(g1,g2)
    c: Vertical(g0)
    c: Vertical(g2)
    c: Horizontal(g1)
    c: DistanceY(g2,g2) = 20
    c: Horizontal(g4)
    c: Horizontal(g3)
    c: Coincident(g2,g4)
    c: Coincident(g0,g3)
    c: DistanceX(g4,g4) = 20
    c: Equal(g4,g3)
    c: Symmetric(g2,g2,g5)
    c: Symmetric(g0,g0,g5)
    c: PointOnObject(g6,g5)
    c: PointOnObject(g7,g5)
    c: Diameter(g6) = 4
    c: DistanceX(g6,g5) = 10
    c: DistanceX(g5,g7) = 10
    c: Equal(g6,g7)
    c: Coincident(g8,g3)
    c: Coincident(g8,g4)
    c: Symmetric(g8,g8,g9)
    c: Symmetric(g-3,g-3,g9)
    c: Vertical(g9)
    c: DistanceY(g9,g9) = 8.2
    c: Horizontal(g8)
    c: Coincident(g10,g3)
    c: Coincident(g10,g-3)
    c: Vertical(g10)
    c: Coincident(g11,g4)
    c: Coincident(g11,g-3)
    c: Coincident(g12,g10)
    c: Coincident(g12,g11)
FEATURE [PartDesign::Pad] Pad012
  BaseFeature = -> Pad006
  Direction = (0,-1,2e-16)
  Length = 10
  Length2 = 10
  Placement = pos=(0,0,0) rot=(1,0,0;1.5708rad)
  Profile = -> Sketch047
  ReferenceAxis = -> Sketch047 [N_Axis]
  Refine = true
  Suppressed = false
  Type = 3
  UpToFace = -> Pad006 [Face6]
FEATURE [PartDesign::Pocket] Pocket022
  BaseFeature = -> Pad012
  Direction = (0,1,-2e-16)
  Length = 1.2
  Length2 = 5
  Placement = pos=(0,0,0) rot=(1,0,0;1.5708rad)
  Profile = -> Sketch044 [Edge2]
  ReferenceAxis = -> Sketch044 [N_Axis]
  Refine = true
  Suppressed = false
  Type = 0
FEATURE [PartDesign::Hole] Hole004
  BaseFeature = -> Pocket022
  CustomThreadClearance = 0
  Depth = 10
  DepthType = 0
  Diameter = 5.4
  DrillForDepth = false
  DrillPoint = 0
  DrillPointAngle = 118
  HoleCutCountersinkAngle = 90
  HoleCutCustomValues = false
  HoleCutDepth = 3
  HoleCutDiameter = 13.3
  HoleCutType = 1
  ModelThread = false
  Placement = pos=(0,0,0) rot=(1,0,0;1.5708rad)
  Profile = -> Pocket022 [Edge44]
  Refine = true
  Reversed = true
  Suppressed = false
  Tapered = false
  TaperedAngle = 90
  ThreadClass = 0
  ThreadDepth = 10
  ThreadDepthType = 0
  ThreadDirection = 0
  ThreadFit = 0
  ThreadSize = 0
  ThreadType = 0
  Threaded = false
  UseCustomThreadClearance = false
FEATURE [Sketcher::SketchObject] Sketch045
  ArcFitTolerance = 1e-06
  AttachmentSupport = -> [Hole004]
  ExternalGeometry = -> [Binder008]
  FullyConstrained = true
  MakeInternals = false
  MapMode = 5
  Placement = pos=(0,6,-2.2e-15) rot=(-1,0,0;1.5708rad)
  sketch-geometry (5):
    g0: Circle CenterX=16.6 CenterY=-33 CenterZ=0 NormalX=0 NormalY=0 NormalZ=1 AngleXU=0 Radius=1.7
    g1: Circle CenterX=-3 CenterY=15 CenterZ=0 NormalX=0 NormalY=0 NormalZ=1 AngleXU=0 Radius=1.7
    g2: Circle CenterX=-3 CenterY=-15 CenterZ=0 NormalX=0 NormalY=0 NormalZ=1 AngleXU=0 Radius=1.7
    g3: Circle CenterX=-12 CenterY=-33 CenterZ=0 NormalX=0 NormalY=0 NormalZ=1 AngleXU=0 Radius=1.7
    g4: Circle CenterX=-12 CenterY=15 CenterZ=0 NormalX=0 NormalY=0 NormalZ=1 AngleXU=0 Radius=1.7
  constraints (10):
    c: Coincident(g0,g-4)
    c: Equal(g0,g-4)
    c: Coincident(g1,g-3)
    c: Equal(g1,g-3)
    c: Coincident(g2,g-6)
    c: Equal(g2,g-6)
    c: Coincident(g3,g-5)
    c: Equal(g3,g-5)
    c: Coincident(g4,g-7)
    c: Equal(g4,g-7)
FEATURE [PartDesign::Hole] Hole005
  BaseFeature = -> Hole004
  CustomThreadClearance = 0
  Depth = 25
  DepthType = 0
  Diameter = 3.2
  DrillForDepth = false
  DrillPoint = 0
  DrillPointAngle = 118
  HoleCutCountersinkAngle = 90
  HoleCutCustomValues = false
  HoleCutDepth = 3.4
  HoleCutDiameter = 5.9
  HoleCutType = 1
  ModelThread = false
  Placement = pos=(0,0,0) rot=(1,0,0;1.5708rad)
  Profile = -> Sketch045
  Refine = true
  Suppressed = false
  Tapered = false
  TaperedAngle = 90
  ThreadClass = 0
  ThreadDepth = 25
  ThreadDepthType = 0
  ThreadDirection = 0
  ThreadFit = 1
  ThreadSize = 9
  ThreadType = 1
  Threaded = false
  UseCustomThreadClearance = false
  expr: HoleCutDiameter = <<Dimensions>>.M3Cap
FEATURE [Sketcher::SketchObject] Sketch046
  ArcFitTolerance = 1e-06
  AttachmentSupport = -> [Hole005]
  ExternalGeometry = -> [Binder008]
  FullyConstrained = true
  MakeInternals = false
  MapMode = 5
  Placement = pos=(0,6,-2.2e-15) rot=(-1,0,0;1.5708rad)
  expr: Constraints[19] = <<Dimensions>>.M3HexW
  sketch-geometry (8):
    g0: LineSegment StartX=17.1546 StartY=14.35 StartZ=0 EndX=20.4454 EndY=14.35 EndZ=0
    g1: LineSegment StartX=20.4454 StartY=14.35 StartZ=0 EndX=22.0909 EndY=17.2 EndZ=0
    g2: LineSegment StartX=22.0909 StartY=17.2 StartZ=0 EndX=20.4454 EndY=20.05 EndZ=0
    g3: LineSegment StartX=20.4454 StartY=20.05 StartZ=0 EndX=17.1546 EndY=20.05 EndZ=0
    g4: LineSegment StartX=17.1546 StartY=20.05 StartZ=0 EndX=15.5091 EndY=17.2 EndZ=0
    g5: LineSegment StartX=15.5091 StartY=17.2 StartZ=0 EndX=17.1546 EndY=14.35 EndZ=0
    g6: Circle [constr] CenterX=18.8 CenterY=17.2 CenterZ=0 NormalX=0 NormalY=0 NormalZ=1 AngleXU=0 Radius=3.2909
    g7: Circle CenterX=18.8 CenterY=17.2 CenterZ=0 NormalX=0 NormalY=0 NormalZ=1 AngleXU=0 Radius=1.69999
  constraints (18):
    c: Coincident(g0,g1)
    c: Coincident(g1,g2)
    c: Coincident(g2,g3)
    c: Coincident(g3,g4)
    c: Coincident(g4,g5)
    c: Coincident(g5,g0)
    c: Equal(g0, g1-g5) x5
    c: PointOnObject(g0,g6)
    c: PointOnObject(g1,g6)
    c: PointOnObject(g2,g6)
    c: PointOnObject(g3,g6)
    c: PointOnObject(g4,g6)
    c: PointOnObject(g5,g6)
    c: Coincident(g6,g-3)
    c: Horizontal(g0)
    c: DistanceY(g0,g2) = 5.7
    c: Coincident(g7,g6)
    c: Tangent(g-3,g7)
FEATURE [PartDesign::Hole] Hole006
  BaseFeature = -> Hole005
  CustomThreadClearance = 0
  Depth = 25
  DepthType = 0
  Diameter = 3.4
  DrillForDepth = false
  DrillPoint = 1
  DrillPointAngle = 118
  HoleCutCountersinkAngle = 90
  HoleCutCustomValues = false
  HoleCutDepth = 3.4
  HoleCutDiameter = 5.9
  HoleCutType = 1
  ModelThread = false
  Placement = pos=(0,0,0) rot=(1,0,0;1.5708rad)
  Profile = -> Sketch046 [Edge7]
  Refine = true
  Suppressed = false
  Tapered = false
  TaperedAngle = 90
  ThreadClass = 0
  ThreadDepth = 25
  ThreadDepthType = 0
  ThreadDirection = 0
  ThreadFit = 0
  ThreadSize = 9
  ThreadType = 1
  Threaded = false
  UseCustomThreadClearance = false
  expr: HoleCutDiameter = <<Dimensions>>.M3Cap
FEATURE [PartDesign::Hole] Hole007  label="Extrusion Hole"
  BaseFeature = -> Hole006
  CustomThreadClearance = 0
  Depth = 10
  DepthType = 0
  Diameter = 4.5
  DrillForDepth = false
  DrillPoint = 0
  DrillPointAngle = 118
  HoleCutCountersinkAngle = 90
  HoleCutCustomValues = false
  HoleCutDepth = 2.2
  HoleCutDiameter = 10.2
  HoleCutType = 1
  ModelThread = false
  Placement = pos=(0,0,0) rot=(1,0,0;1.5708rad)
  Profile = -> Hole006 [Edge28,Edge21]
  Refine = true
  Reversed = true
  Suppressed = false
  Tapered = false
  TaperedAngle = 90
  ThreadClass = 0
  ThreadDepth = 10
  ThreadDepthType = 0
  ThreadDirection = 0
  ThreadFit = 0
  ThreadSize = 11
  ThreadType = 1
  Threaded = false
  UseCustomThreadClearance = false
FEATURE [PartDesign::Fillet] Fillet037
  Base = -> Hole007 [Edge48,Edge50,Edge10,Edge7,Edge47,Edge51,Edge49,Edge52,Edge2,Edge1]
  BaseFeature = -> Hole007
  Placement = pos=(0,0,0) rot=(1,0,0;1.5708rad)
  Radius = 4
  Refine = true
  SupportTransform = false
  Suppressed = false
  UseAllEdges = false
FEATURE [PartDesign::Fillet] Fillet038
  Base = -> Fillet037 [Edge84]
  BaseFeature = -> Fillet037
  Placement = pos=(0,0,0) rot=(1,0,0;1.5708rad)
  Radius = 4.5
  Refine = true
  SupportTransform = false
  Suppressed = false
  UseAllEdges = false
FEATURE [PartDesign::Fillet] Fillet039
  Base = -> Fillet038 [Edge40]
  BaseFeature = -> Fillet038
  Placement = pos=(0,0,0) rot=(1,0,0;1.5708rad)
  Radius = 6.5
  Refine = true
  SupportTransform = false
  Suppressed = false
  UseAllEdges = false
FEATURE [PartDesign::Pad] Pad013
  BaseFeature = -> Pocket017
  Direction = (0,1,0)
  Length = 0.4
  Length2 = 10
  Placement = pos=(0,0,0) rot=(0,-1,0;1.5708rad)
  Profile = -> Pocket017 [Edge164]
  Refine = true
  Suppressed = false
  Type = 0
FEATURE [PartDesign::Body] Body
  AllowCompound = false
  Group = -> [Binder,Sketch001,Pad,Sketch002,Pocket,Sketch003,Hole,Hole001,Sketch004,Pocket001,Sketch005,Pad001,Fillet,Chamfer,Chamfer002,Binder006,Sketch023,Pocket009,Sketch025,Pocket013,Sketch026,Pocket014,Pad004,Fillet008,Fillet009,Fillet016,Chamfer009,Sketch030,Pocket017,Pad013]
  Origin = -> Origin001
  Tip = -> Pad013
FEATURE [App::Part] Part  label="MotorMount"
  Group = -> [Body]
  Origin = -> Origin
  Placement = pos=(0,0,0) rot=(0,1,0;4.71239rad)
FEATURE [PartDesign::Fillet] Fillet040
  Base = -> Pocket021 [Edge43]
  BaseFeature = -> Pocket021
  Placement = pos=(0,0,0) rot=(1,0,0;1.5708rad)
  Radius = 6
  Refine = true
  SupportTransform = false
  Suppressed = false
  UseAllEdges = false
FEATURE [PartDesign::Fillet] Fillet041
  Base = -> Fillet040 [Edge48]
  BaseFeature = -> Fillet040
  Placement = pos=(0,0,0) rot=(1,0,0;1.5708rad)
  Radius = 32
  Refine = true
  SupportTransform = false
  Suppressed = false
  UseAllEdges = false
FEATURE [PartDesign::Fillet] Fillet042
  Base = -> Fillet041 [Edge39,Edge35]
  BaseFeature = -> Fillet041
  Placement = pos=(0,0,0) rot=(1,0,0;1.5708rad)
  Radius = 1
  Refine = true
  SupportTransform = false
  Suppressed = false
  UseAllEdges = false
FEATURE [PartDesign::Body] Body008  label="Latch-Body008"
  AllowCompound = false
  Group = -> [Binder011,Sketch040,Pad010,Fillet029,Fillet030,Fillet031,Fillet032,Fillet033,Fillet034,Sketch043,Pocket021,Fillet040,Fillet041,Fillet042]
  Origin = -> Origin030
  Placement = pos=(-0.4,0,0.1) rot=(0,0,1;0rad)
  Tip = -> Fillet042
FEATURE [App::Part] Part006  label="TensionerLatch"
  Group = -> [Body008]
  Origin = -> Origin029
FEATURE [Sketcher::SketchObject] Sketch048  label="FilamentHole"
  ArcFitTolerance = 1e-06
  AttachmentSupport = -> [Fillet025]
  ExternalGeometry = -> [Binder010]
  FullyConstrained = true
  MakeInternals = false
  MapMode = 5
  Placement = pos=(0,-1.1e-14,-31.3) rot=(1,0,0;3.14159rad)
  sketch-geometry (1):
    g0: Circle CenterX=6.25 CenterY=-15.85 CenterZ=0 NormalX=0 NormalY=0 NormalZ=1 AngleXU=0 Radius=4.75
  constraints (2):
    c: Coincident(g0,g-3)
    c: Diameter(g0) = 9.5
FEATURE [Sketcher::SketchObject] Sketch049
  ArcFitTolerance = 1e-06
  ExternalGeometry = -> [Binder010]
  FullyConstrained = true
  MakeInternals = false
  MapMode = 5
  Placement = pos=(0,8.8e-15,39.5) rot=(0,0,1;3.14159rad)
  sketch-geometry (1):
    g0: Circle CenterX=-6.25 CenterY=-15.85 CenterZ=0 NormalX=0 NormalY=0 NormalZ=1 AngleXU=0 Radius=4.75
  constraints (2):
    c: Coincident(g0,g-3)
    c: Diameter(g0) = 9.5
FEATURE [PartDesign::Pocket] Pocket024  label="TopFilamentPath"
  BaseFeature = -> Fillet025
  Direction = (0,0,-1)
  Length = 6
  Length2 = 5
  Placement = pos=(0,0,0) rot=(1,0,0;1.5708rad)
  Profile = -> Sketch049
  ReferenceAxis = -> Sketch049 [N_Axis]
  Refine = true
  Suppressed = false
  Type = 0
FEATURE [PartDesign::SubShapeBinder] Binder012  label="TensionerAxleCutoutBinder"
  BindCopyOnChange = 0
  BindMode = 0
  ClaimChildren = false
  Context = -> Part005 [Body007.Binder012.]
  Fuse = false
  MakeFace = true
  OffsetFill = false
  OffsetIntersection = false
  OffsetJoinType = 0
  OffsetOpenResult = false
  PartialLoad = false
  Refine = true
  Relative = true
  Support = -> [Part[Body.Pad013.Face7]]
  _Version = 2
FEATURE [Sketcher::SketchObject] Sketch050
  ArcFitTolerance = 1e-06
  AttachmentSupport = -> [Fillet039]
  ExternalGeometry = -> [Binder012]
  FullyConstrained = true
  MakeInternals = false
  MapMode = 5
  Placement = pos=(0,3e-16,0) rot=(1,0,0;1.5708rad)
  sketch-geometry (4):
    g0: ArcOfCircle CenterX=12.666 CenterY=8e-15 CenterZ=0 NormalX=0 NormalY=0 NormalZ=1 AngleXU=0 Radius=2.5 StartAngle=1.5708 EndAngle=4.2461
    g1: LineSegment StartX=12.666 StartY=2.5 StartZ=0 EndX=24.666 EndY=2.5 EndZ=0
    g2: LineSegment StartX=11.5421 StartY=-2.2331 StartZ=0 EndX=24.666 EndY=-8.83851 EndZ=0
    g3: LineSegment StartX=24.666 StartY=2.5 StartZ=0 EndX=24.666 EndY=-8.83851 EndZ=0
  constraints (10):
    c: Coincident(g0,g-3)
    c: Coincident(g0,g-3)
    c: Coincident(g1,g0)
    c: Horizontal(g1)
    c: Tangent(g2,g0) = -1.5708
    c: Coincident(g3,g1)
    c: Coincident(g3,g2)
    c: Vertical(g3)
    c: DistanceX(g1,g1) = 12
    c: Parallel(g-4,g2)
FEATURE [PartDesign::Pocket] Pocket025  label="AxleCutOutPocket"
  BaseFeature = -> Fillet039
  Direction = (0,1,-2e-16)
  Length = 2
  Length2 = 5
  Placement = pos=(0,0,0) rot=(1,0,0;1.5708rad)
  Profile = -> Sketch050
  ReferenceAxis = -> Sketch050 [N_Axis]
  Refine = true
  Suppressed = false
  Type = 0
FEATURE [PartDesign::Pad] Pad014  label="ScrewSupports"
  BaseFeature = -> Pocket025
  Direction = (0,1,0)
  Length = 0.4
  Length2 = 10
  Placement = pos=(0,0,0) rot=(1,0,0;1.5708rad)
  Profile = -> Pocket025 [Edge103,Edge101,Edge95,Edge107,Edge99,Edge109]
  Refine = true
  Reversed = true
  Suppressed = false
  Type = 0
FEATURE [PartDesign::Chamfer] Chamfer012  label="EdgeChamfer"
  Angle = 45
  Base = -> Pad014 [Edge93]
  BaseFeature = -> Pad014
  ChamferType = 0
  FlipDirection = false
  Placement = pos=(0,0,0) rot=(1,0,0;1.5708rad)
  Refine = true
  Size = 1
  Size2 = 1
  SupportTransform = false
  Suppressed = false
  UseAllEdges = false
FEATURE [PartDesign::Body] Body005  label="Back Plate Body"
  AllowCompound = false
  Group = -> [Sketch027,Binder008,Pad006,Pad012,Sketch047,Sketch044,Pocket022,Hole004,Sketch045,Hole005,Sketch046,Hole006,Hole007,Fillet037,Fillet038,Fillet039,Binder012,Sketch050,Pocket025,Pad014,Chamfer012]
  Origin = -> Origin025
  Placement = pos=(0,22,0) rot=(0,0,1;0rad)
  Tip = -> Chamfer012
FEATURE [App::Part] Part004  label="BackPlateBowden"
  Group = -> [Body005]
  Origin = -> Origin024
FEATURE [Sketcher::SketchObject] Sketch051
  ArcFitTolerance = 1e-06
  AttachmentSupport = -> [Fillet028]
  ExternalGeometry = -> [Fillet028]
  FullyConstrained = true
  MakeInternals = false
  MapMode = 5
  Placement = pos=(23.05,0,0) rot=(0.707107,0,0.707107;3.14159rad)
  sketch-geometry (5):
    g0: ArcOfCircle CenterX=22 CenterY=-5 CenterZ=0 NormalX=0 NormalY=0 NormalZ=1 AngleXU=0 Radius=1.7 StartAngle=1.5708 EndAngle=4.71239
    g1: LineSegment StartX=22 StartY=-6.7 StartZ=0 EndX=26 EndY=-6.7 EndZ=0
    g2: LineSegment StartX=22 StartY=-3.3 StartZ=0 EndX=26 EndY=-3.3 EndZ=0
    g3: LineSegment [constr] StartX=22 StartY=-3.3 StartZ=0 EndX=22 EndY=-6.7 EndZ=0
    g4: LineSegment StartX=26 StartY=-3.3 StartZ=0 EndX=26 EndY=-6.7 EndZ=0
  constraints (13):
    c: Diameter(g0) = 3.4
    c: DistanceY(g0,g-1) = 5
    c: PointOnObject(g1,g-3)
    c: Horizontal(g1)
    c: PointOnObject(g2,g-3)
    c: Horizontal(g2)
    c: Tangent(g0,g1) = -1.5708
    c: Tangent(g0,g2) = 1.5708
    c: Coincident(g3,g0)
    c: Coincident(g3,g0)
    c: DistanceX(g-1,g0) = 22
    c: Coincident(g4,g2)
    c: Coincident(g4,g1)
FEATURE [PartDesign::Pocket] Pocket026
  BaseFeature = -> Fillet028
  Direction = (-1,0,2e-16)
  Length = 10
  Length2 = 5
  Placement = pos=(0,0,0) rot=(1,0,0;1.5708rad)
  Profile = -> Sketch051
  ReferenceAxis = -> Sketch051 [N_Axis]
  Refine = true
  Suppressed = false
  Type = 0
FEATURE [PartDesign::Chamfer] Chamfer013
  Angle = 45
  Base = -> Pocket026 [Edge98,Edge100]
  BaseFeature = -> Pocket026
  ChamferType = 0
  FlipDirection = false
  Placement = pos=(0,0,0) rot=(1,0,0;1.5708rad)
  Refine = true
  Size = 1
  Size2 = 1
  SupportTransform = false
  Suppressed = false
  UseAllEdges = false
FEATURE [PartDesign::Body] Body003  label="Tensioner Body"
  AllowCompound = false
  Group = -> [Binder003,Sketch013,Binder004,Pad003,Sketch015,Pocket005,Sketch016,Sketch017,Hole003,Sketch018,Pocket007,Fillet026,Fillet027,Fillet028,Sketch051,Pocket026,Chamfer013]
  Origin = -> Origin022
  Tip = -> Chamfer013
FEATURE [App::Part] Part003  label="TensionerGeared"
  Group = -> [Body003]
  Origin = -> Origin021
FEATURE [Sketcher::SketchObject] Sketch052
  ArcFitTolerance = 1e-06
  AttachmentSupport = -> [Fillet035]
  ExternalGeometry = -> [Fillet035]
  FullyConstrained = true
  MakeInternals = false
  MapMode = 5
  Placement = pos=(14.1697,0,0) rot=(0.707107,0,0.707107;3.14159rad)
  expr: Constraints[0] = <<Dimensions>>.M3HeatSetW
  sketch-geometry (3):
    g0: Circle CenterX=24.0892 CenterY=-4.75 CenterZ=0 NormalX=0 NormalY=0 NormalZ=1 AngleXU=0 Radius=2.75
    g1: LineSegment [constr] StartX=19.6096 StartY=-4.75 StartZ=0 EndX=24.0892 EndY=-4.75 EndZ=0
    g2: LineSegment [constr] StartX=24.0892 StartY=-9.5 StartZ=0 EndX=24.0892 EndY=-4.75 EndZ=0
  constraints (7):
    c: Diameter(g0) = 5.5
    c: Symmetric(g-4,g-4,g1)
    c: Coincident(g1,g0)
    c: Symmetric(g-3,g-3,g2)
    c: Coincident(g2,g0)
    c: Vertical(g2)
    c: Horizontal(g1)
FEATURE [PartDesign::Pocket] Pocket027
  BaseFeature = -> Fillet035
  Direction = (-1,0,2e-16)
  Length = 4
  Length2 = 5
  Placement = pos=(0,0,0) rot=(1,0,0;1.5708rad)
  Profile = -> Sketch052
  ReferenceAxis = -> Sketch052 [N_Axis]
  Refine = true
  Suppressed = false
  Type = 0
  expr: Length = <<Dimensions>>.M3HeatSetD
FEATURE [PartDesign::Fillet] Fillet043
  Base = -> Pocket027 [Edge24,Edge23]
  BaseFeature = -> Pocket027
  Placement = pos=(0,0,0) rot=(1,0,0;1.5708rad)
  Radius = 1
  Refine = true
  SupportTransform = false
  Suppressed = false
  UseAllEdges = false
FEATURE [PartDesign::Fillet] Fillet044
  Base = -> Fillet043 [Edge12]
  BaseFeature = -> Fillet043
  Placement = pos=(0,0,0) rot=(1,0,0;1.5708rad)
  Radius = 2
  Refine = true
  SupportTransform = false
  Suppressed = false
  UseAllEdges = false
FEATURE [PartDesign::Hole] Hole010
  BaseFeature = -> Fillet044
  CustomThreadClearance = 0
  Depth = 20
  DepthType = 0
  Diameter = 3.4
  DrillForDepth = false
  DrillPoint = 0
  DrillPointAngle = 118
  HoleCutCountersinkAngle = 90
  HoleCutCustomValues = false
  HoleCutDepth = 0
  HoleCutDiameter = 6.1
  HoleCutType = 0
  ModelThread = false
  Placement = pos=(0,0,0) rot=(1,0,0;1.5708rad)
  Profile = -> Fillet044 [Edge36]
  Refine = true
  Suppressed = false
  Tapered = false
  TaperedAngle = 90
  ThreadClass = 0
  ThreadDepth = 20
  ThreadDepthType = 0
  ThreadDirection = 0
  ThreadFit = 0
  ThreadSize = 9
  ThreadType = 1
  Threaded = false
  UseCustomThreadClearance = false
FEATURE [Sketcher::SketchObject] Sketch053
  ArcFitTolerance = 1e-06
  AttachmentSupport = -> [Hole010]
  ExternalGeometry = -> [Hole010]
  FullyConstrained = true
  MakeInternals = false
  MapMode = 5
  Placement = pos=(0,9.5,0) rot=(-1,0,0;1.5708rad)
  sketch-geometry (4):
    g0: LineSegment StartX=14.1697 StartY=-26.1096 StartZ=0 EndX=5.16969 EndY=-26.1096 EndZ=0
    g1: LineSegment StartX=5.16969 StartY=-26.1096 StartZ=0 EndX=5.16969 EndY=-22.6096 EndZ=0
    g2: LineSegment StartX=5.16969 StartY=-22.6096 StartZ=0 EndX=14.1697 EndY=-22.6096 EndZ=0
    g3: LineSegment StartX=14.1697 StartY=-22.6096 StartZ=0 EndX=14.1697 EndY=-26.1096 EndZ=0
  constraints (12):
    c: PointOnObject(g0,g-3)
    c: Horizontal(g0)
    c: Coincident(g0,g1)
    c: Vertical(g1)
    c: Coincident(g1,g2)
    c: PointOnObject(g2,g-3)
    c: Horizontal(g2)
    c: Coincident(g2,g3)
    c: Coincident(g3,g0)
    c: DistanceY(g3,g3) = 3.5
    c: DistanceX(g2,g2) = 9
    c: DistanceY(g2,g-4) = 3
FEATURE [PartDesign::Pad] Pad015
  BaseFeature = -> Hole010
  Direction = (0,1,2e-16)
  Length = 2
  Length2 = 10
  Placement = pos=(0,0,0) rot=(1,0,0;1.5708rad)
  Profile = -> Sketch053
  ReferenceAxis = -> Sketch053 [N_Axis]
  Refine = true
  Suppressed = false
  Type = 0
FEATURE [PartDesign::Fillet] Fillet045
  Base = -> Pad015 [Edge41]
  BaseFeature = -> Pad015
  Placement = pos=(0,0,0) rot=(1,0,0;1.5708rad)
  Radius = 1.5
  Refine = true
  SupportTransform = false
  Suppressed = false
  UseAllEdges = false
FEATURE [PartDesign::Chamfer] Chamfer014
  Angle = 45
  Base = -> Fillet045 [Edge23]
  BaseFeature = -> Fillet045
  ChamferType = 0
  FlipDirection = false
  Placement = pos=(0,0,0) rot=(1,0,0;1.5708rad)
  Refine = true
  Size = 1.98
  Size2 = 1
  SupportTransform = false
  Suppressed = false
  UseAllEdges = false
FEATURE [PartDesign::Body] Body009
  AllowCompound = false
  Group = -> [Sketch042,Pad011,Fillet035,Sketch052,Pocket027,Fillet043,Fillet044,Hole010,Sketch053,Pad015,Fillet045,Chamfer014]
  Origin = -> Origin033
  Tip = -> Chamfer014
FEATURE [App::Part] Part007  label="LatchShuttle"
  Group = -> [Body009]
  Origin = -> Origin032
FEATURE [PartDesign::SubShapeBinder] Binder013  label="BodyScrewsBinder"
  BindCopyOnChange = 0
  BindMode = 0
  ClaimChildren = false
  Context = -> Part008 [Body010.Binder013.]
  Fuse = false
  MakeFace = true
  OffsetFill = false
  OffsetIntersection = false
  OffsetJoinType = 0
  OffsetOpenResult = false
  PartialLoad = false
  Refine = true
  Relative = true
  Support = -> [Sketch014]
  _Version = 2
FEATURE [PartDesign::SubShapeBinder] Binder014  label="FilamentPathBinder014"
  BindCopyOnChange = 0
  BindMode = 0
  ClaimChildren = false
  Context = -> Part008 [Body010.Binder014.]
  Fuse = false
  MakeFace = true
  OffsetFill = false
  OffsetIntersection = false
  OffsetJoinType = 0
  OffsetOpenResult = false
  PartialLoad = false
  Refine = true
  Relative = true
  Support = -> [Sketch006]
  _Version = 2
FEATURE [Sketcher::SketchObject] Sketch054
  ArcFitTolerance = 1e-06
  AttachmentSupport = -> [XZ_Plane035]
  ExternalGeometry = -> [Binder013,Binder014]
  FullyConstrained = true
  MakeInternals = false
  MapMode = 5
  Placement = pos=(0,0,0) rot=(1,0,0;1.5708rad)
  sketch-geometry (15):
    g0: Circle [constr] CenterX=18.8 CenterY=-17.2 CenterZ=0 NormalX=0 NormalY=0 NormalZ=1 AngleXU=0 Radius=4.25
    g1: LineSegment StartX=14.55 StartY=-17.2 StartZ=0 EndX=14.55 EndY=-5.59308 EndZ=0
    g2: LineSegment StartX=14.55 StartY=26 StartZ=0 EndX=23.05 EndY=26 EndZ=0
    g3: LineSegment StartX=23.05 StartY=26 StartZ=0 EndX=23.05 EndY=-17.2 EndZ=0
    g4: Circle CenterX=18.8 CenterY=-17.2 CenterZ=0 NormalX=0 NormalY=0 NormalZ=1 AngleXU=0 Radius=1.7
    g5: LineSegment [constr] StartX=14.55 StartY=-17.2 StartZ=0 EndX=23.05 EndY=-17.2 EndZ=0
    g6: Circle [constr] CenterX=13.75 CenterY=0 CenterZ=0 NormalX=0 NormalY=0 NormalZ=1 AngleXU=0 Radius=8
    g7: GeomPoint X=5.75 Y=3.5e-15 Z=0
    g8: GeomPoint X=6.25 Y=3.5e-15 Z=0
    g9: Circle CenterX=13.75 CenterY=0 CenterZ=0 NormalX=0 NormalY=0 NormalZ=1 AngleXU=0 Radius=2.65
    g10: Circle [constr] CenterX=13.75 CenterY=0 CenterZ=0 NormalX=0 NormalY=0 NormalZ=1 AngleXU=0 Radius=5.65
    g11: LineSegment StartX=14.55 StartY=5.59308 StartZ=0 EndX=14.55 EndY=26 EndZ=0
    g12: ArcOfCircle CenterX=13.75 CenterY=0 CenterZ=0 NormalX=0 NormalY=0 NormalZ=1 AngleXU=0 Radius=5.65 StartAngle=1.42873 EndAngle=4.85446
    g13: LineSegment [constr] StartX=14.55 StartY=5.59308 StartZ=0 EndX=14.55 EndY=-5.59308 EndZ=0
    g14: ArcOfCircle CenterX=18.8 CenterY=-17.2 CenterZ=0 NormalX=0 NormalY=0 NormalZ=1 AngleXU=0 Radius=4.25 StartAngle=3.14159 EndAngle=6.28319
  constraints (36):
    c: Coincident(g0,g-3)
    c: Vertical(g1)
    c: Tangent(g1,g0)
    c: Coincident(g11,g2)
    c: Horizontal(g2)
    c: Coincident(g2,g3)
    c: Vertical(g3)
    c: Diameter(g0) = 8.5
    c: Coincident(g4,g0)
    c: Diameter(g4) = 3.4
    c: Symmetric(g1,g3,g0)
    c: DistanceY(g3,g3) = 43.2
    c: Diameter(g6) = 16
    c: PointOnObject(g6,g-1)
    c: PointOnObject(g7,g6)
    c: PointOnObject(g7,g-4)
    c: Symmetric(g-4,g-4,g8)
    c: Coincident(g9,g6)
    c: Diameter(g9) = 5.3
    c: Coincident(g10,g6)
    c: Distance(g10,g9) = 3
    c: PointOnObject(g11,g10)
    c: Coincident(g12,g6)
    c: Coincident(g12,g11)
    c: Coincident(g12,g1)
    c: Vertical(g11)
    c: Coincident(g13,g1)
    c: Coincident(g13,g11)
    c: Vertical(g13)
    c: Coincident(g14,g1)
    c: Coincident(g14,g0)
    c: Coincident(g3,g5)
    c: Horizontal(g5)
    c: Coincident(g5,g1)
    c: Angle(g14) = 3.14159
    c: DistanceX(g7,g8) = 0.5
FEATURE [PartDesign::Pad] Pad016  label="TensionerBase"
  Direction = (0,-1,2e-16)
  Length = 22
  Length2 = 10
  Placement = pos=(0,0,0) rot=(1,0,0;1.5708rad)
  Profile = -> Sketch054
  ReferenceAxis = -> Sketch054 [N_Axis]
  Refine = true
  Reversed = true
  Suppressed = false
  Type = 0
FEATURE [PartDesign::Plane] DatumPlane  label="MidPlane"
  AttachmentOffset = pos=(0,0,0) rot=(0,1,0;1.5708rad)
  AttachmentSupport = -> [Binder014]
  Length = 61.0995
  MapMode = 11
  Placement = pos=(6.25,15.85,0) rot=(-0.57735,0.57735,0.57735;2.0944rad)
  ResizeMode = 0
  Width = 60.0995
FEATURE [Sketcher::SketchObject] Sketch055
  ArcFitTolerance = 1e-06
  AttachmentSupport = -> [DatumPlane]
  ExternalGeometry = -> [Pad016]
  FullyConstrained = true
  MakeInternals = false
  MapMode = 5
  Placement = pos=(6.25,15.85,0) rot=(0.57735,-0.57735,-0.57735;4.18879rad)
  sketch-geometry (1):
    g0: Circle CenterX=4.9e-15 CenterY=-7.5 CenterZ=0 NormalX=0 NormalY=0 NormalZ=1 AngleXU=0 Radius=9.5
  constraints (2):
    c: Coincident(g0,g-3)
    c: Diameter(g0) = 19
FEATURE [PartDesign::Pocket] Pocket028
  BaseFeature = -> Pad016
  Direction = (0,-1,0)
  Length = 5.5
  Length2 = 5
  Midplane = true
  Placement = pos=(0,0,0) rot=(1,0,0;1.5708rad)
  Profile = -> Sketch055
  ReferenceAxis = -> Sketch055 [N_Axis]
  Refine = true
  Suppressed = false
  Type = 0
FEATURE [Sketcher::SketchObject] Sketch056
  ArcFitTolerance = 1e-06
  AttachmentSupport = -> [Pocket028]
  ExternalGeometry = -> [Pocket028]
  FullyConstrained = true
  MakeInternals = false
  MapMode = 5
  Placement = pos=(23.05,0,0) rot=(0.707107,0,0.707107;3.14159rad)
  sketch-geometry (6):
    g0: Circle [constr] CenterX=22 CenterY=-5 CenterZ=0 NormalX=0 NormalY=0 NormalZ=1 AngleXU=0 Radius=1.7
    g1: LineSegment StartX=26 StartY=-3.3 StartZ=0 EndX=22 EndY=-3.3 EndZ=0
    g2: LineSegment StartX=22 StartY=-6.7 StartZ=0 EndX=26 EndY=-6.7 EndZ=0
    g3: LineSegment StartX=26 StartY=-6.7 StartZ=0 EndX=26 EndY=-3.3 EndZ=0
    g4: LineSegment [constr] StartX=22 StartY=-3.3 StartZ=0 EndX=22 EndY=-6.7 EndZ=0
    g5: ArcOfCircle CenterX=22 CenterY=-5 CenterZ=0 NormalX=0 NormalY=0 NormalZ=1 AngleXU=0 Radius=1.7 StartAngle=1.5708 EndAngle=4.71239
  constraints (16):
    c: PointOnObject(g1,g-3)
    c: Tangent(g1,g0) = -1.5708
    c: Horizontal(g1)
    c: Tangent(g2,g0) = -1.5708
    c: PointOnObject(g2,g-3)
    c: Horizontal(g2)
    c: Coincident(g3,g2)
    c: Coincident(g3,g1)
    c: Coincident(g4,g1)
    c: Coincident(g4,g2)
    c: Coincident(g5,g0)
    c: Coincident(g5,g1)
    c: Angle(g5) = 3.14159
    c: DistanceY(g1,g-3) = 3.3
    c: DistanceY(g2,g1) = 3.4
    c: DistanceX(g2,g2) = 4
FEATURE [PartDesign::Pocket] Pocket029
  BaseFeature = -> Pocket028
  Direction = (-1,0,2e-16)
  Length = 10
  Length2 = 5
  Placement = pos=(0,0,0) rot=(1,0,0;1.5708rad)
  Profile = -> Sketch056
  ReferenceAxis = -> Sketch056 [N_Axis]
  Refine = true
  Suppressed = false
  Type = 0
FEATURE [PartDesign::Plane] DatumPlane001
  AttachmentOffset = pos=(0,0,-7.65) rot=(0,0,1;0rad)
  AttachmentSupport = -> [Pocket029]
  Length = 60.0995
  MapMode = 5
  Placement = pos=(0,14.35,-1.7e-15) rot=(-1,0,0;1.5708rad)
  ResizeMode = 0
  Width = 61.0995
  expr: .AttachmentOffset.Base.z = -15.3 mm / 2 mm
FEATURE [Sketcher::SketchObject] Sketch057
  ArcFitTolerance = 1e-06
  AttachmentSupport = -> [DatumPlane001]
  ExternalGeometry = -> [Pocket029]
  FullyConstrained = true
  MakeInternals = false
  MapMode = 5
  Placement = pos=(0,14.35,-1.7e-15) rot=(-1,0,0;1.5708rad)
  sketch-geometry (3):
    g0: LineSegment StartX=14.55 StartY=-26 StartZ=0 EndX=19.05 EndY=-26 EndZ=0
    g1: LineSegment StartX=19.05 StartY=-26 StartZ=0 EndX=14.55 EndY=-10.5 EndZ=0
    g2: LineSegment StartX=14.55 StartY=-10.5 StartZ=0 EndX=14.55 EndY=-26 EndZ=0
  constraints (8):
    c: Coincident(g-4,g0)
    c: PointOnObject(g0,g-3)
    c: Coincident(g0,g1)
    c: PointOnObject(g1,g-4)
    c: Coincident(g1,g2)
    c: Coincident(g2,g0)
    c: DistanceY(g2,g2) = 15.5
    c: DistanceX(g0,g0) = 4.5
FEATURE [PartDesign::Pocket] Pocket030  label="FingerTab"
  BaseFeature = -> Pocket029
  Direction = (0,-1,-2e-16)
  Length = 9
  Length2 = 5
  Midplane = true
  Placement = pos=(0,0,0) rot=(1,0,0;1.5708rad)
  Profile = -> Sketch057
  ReferenceAxis = -> Sketch057 [N_Axis]
  Refine = true
  Suppressed = false
  Type = 0
FEATURE [Sketcher::SketchObject] Sketch058
  ArcFitTolerance = 1e-06
  AttachmentSupport = -> [Pocket030]
  ExternalGeometry = -> [Pocket030]
  FullyConstrained = true
  MakeInternals = false
  MapMode = 5
  Placement = pos=(0,22,0) rot=(-1,0,0;1.5708rad)
  sketch-geometry (3):
    g0: LineSegment StartX=23.05 StartY=17.2 StartZ=0 EndX=23.05 EndY=18.9604 EndZ=0
    g1: LineSegment StartX=23.05 StartY=18.9604 StartZ=0 EndX=21.8052 EndY=20.2052 EndZ=0
    g2: LineSegment StartX=21.8052 StartY=20.2052 StartZ=0 EndX=23.05 EndY=17.2 EndZ=0
  constraints (7):
    c: Coincident(g-4,g0)
    c: Coincident(g0,g1)
    c: Coincident(g1,g2)
    c: Coincident(g2,g0)
    c: Vertical(g0)
    c: Tangent(g1,g-4) = -1.5708
    c: Angle(g0,g1) = 0.785398
FEATURE [PartDesign::Pad] Pad017
  BaseFeature = -> Pocket030
  Direction = (0,1,2e-16)
  Length = 15
  Length2 = 10
  Placement = pos=(0,0,0) rot=(1,0,0;1.5708rad)
  Profile = -> Sketch058
  ReferenceAxis = -> Sketch058 [N_Axis]
  Refine = true
  Reversed = true
  Suppressed = false
  Type = 3
  UpToFace = -> Pocket030 [Face2]
FEATURE [PartDesign::Fillet] Fillet046
  Base = -> Pad017 [Edge4,Edge9,Edge13,Edge19,Edge15,Edge25,Edge21]
  BaseFeature = -> Pad017
  Placement = pos=(0,0,0) rot=(1,0,0;1.5708rad)
  Radius = 3
  Refine = true
  SupportTransform = false
  Suppressed = false
  UseAllEdges = false
FEATURE [PartDesign::Chamfer] Chamfer015
  Angle = 45
  Base = -> Fillet046 [Edge3,Edge20,Edge25,Edge27]
  BaseFeature = -> Fillet046
  ChamferType = 0
  FlipDirection = false
  Placement = pos=(0,0,0) rot=(1,0,0;1.5708rad)
  Refine = true
  Size = 1
  Size2 = 1
  SupportTransform = false
  Suppressed = false
  UseAllEdges = false
FEATURE [PartDesign::Body] Body010  label="BearingTensionerBody"
  AllowCompound = false
  Group = -> [Binder013,Binder014,Sketch054,Pad016,DatumPlane,Sketch055,Pocket028,Sketch056,Pocket029,DatumPlane001,Sketch057,Pocket030,Sketch058,Pad017,Fillet046,Chamfer015]
  Origin = -> Origin035
  Tip = -> Chamfer015
FEATURE [App::Part] Part008  label="TensionerBearing"
  Group = -> [Body010]
  Origin = -> Origin034
FEATURE [Sketcher::SketchObject] Sketch059
  ArcFitTolerance = 1e-06
  AttachmentSupport = -> [XZ_Plane037]
  FullyConstrained = false
  MakeInternals = false
  MapMode = 5
  Placement = pos=(0,0,0) rot=(1,0,0;1.5708rad)
  sketch-geometry (2):
    g0: Circle CenterX=14.9831 CenterY=0 CenterZ=0 NormalX=0 NormalY=0 NormalZ=1 AngleXU=0 Radius=8
    g1: Circle CenterX=14.9831 CenterY=0 CenterZ=0 NormalX=0 NormalY=0 NormalZ=1 AngleXU=0 Radius=2.5
  constraints (4):
    c: PointOnObject(g0,g-1)
    c: Diameter(g0) = 16
    c: Coincident(g1,g0)
    c: Diameter(g1) = 5
FEATURE [PartDesign::Pad] Pad018
  Direction = (0,-1,2e-16)
  Length = 5
  Length2 = 10
  Placement = pos=(0,0,0) rot=(1,0,0;1.5708rad)
  Profile = -> Sketch059
  ReferenceAxis = -> Sketch059 [N_Axis]
  Refine = true
  Suppressed = false
  Type = 0
FEATURE [PartDesign::Chamfer] Chamfer016
  Angle = 45
  Base = -> Pad018 [Edge3,Edge6,Edge5,Edge2]
  BaseFeature = -> Pad018
  ChamferType = 0
  FlipDirection = false
  Placement = pos=(0,0,0) rot=(1,0,0;1.5708rad)
  Refine = true
  Size = 0.5
  Size2 = 1
  SupportTransform = false
  Suppressed = false
  UseAllEdges = false
FEATURE [PartDesign::Body] Body011
  AllowCompound = false
  Group = -> [Sketch059,Pad018,Chamfer016]
  Origin = -> Origin037
  Tip = -> Chamfer016
FEATURE [App::Part] Part009  label="625TensionerBearing"
  Group = -> [Body011]
  Origin = -> Origin036
  Placement = pos=(-0.6,18.3,0) rot=(0,0,1;0rad)
FEATURE [Sketcher::SketchObject] Sketch060
  ArcFitTolerance = 1e-06
  AttachmentSupport = -> [XZ_Plane039]
  FullyConstrained = true
  MakeInternals = false
  MapMode = 5
  Placement = pos=(0,0,0) rot=(1,0,0;1.5708rad)
  sketch-geometry (2):
    g0: ArcOfCircle CenterX=0 CenterY=0 CenterZ=0 NormalX=0 NormalY=0 NormalZ=1 AngleXU=0 Radius=2.55 StartAngle=5.52683 EndAngle=10.1811
    g1: LineSegment StartX=-1.85472 StartY=-1.75 StartZ=0 EndX=1.85472 EndY=-1.75 EndZ=0
  constraints (6):
    c: Coincident(g0,g-1)
    c: Diameter(g0) = 5.1
    c: Horizontal(g1)
    c: DistanceY(g1,g0) = 1.75
    c: Coincident(g0,g1)
    c: Coincident(g0,g1)
FEATURE [PartDesign::Pad] Pad019
  Direction = (0,-1,2e-16)
  Length = 22
  Length2 = 10
  Placement = pos=(0,0,0) rot=(1,0,0;1.5708rad)
  Profile = -> Sketch060
  ReferenceAxis = -> Sketch060 [N_Axis]
  Refine = true
  Reversed = true
  Suppressed = false
  Type = 0
FEATURE [PartDesign::Chamfer] Chamfer017
  Angle = 45
  Base = -> Pad019 [Edge4,Edge3]
  BaseFeature = -> Pad019
  ChamferType = 0
  FlipDirection = false
  Placement = pos=(0,0,0) rot=(1,0,0;1.5708rad)
  Refine = true
  Size = 0.5
  Size2 = 1
  SupportTransform = false
  Suppressed = false
  UseAllEdges = false
FEATURE [PartDesign::SubShapeBinder] Binder015
  BindCopyOnChange = 0
  BindMode = 0
  ClaimChildren = false
  Context = -> Part010 [Body012.Binder015.]
  Fuse = false
  MakeFace = true
  OffsetFill = false
  OffsetIntersection = false
  OffsetJoinType = 0
  OffsetOpenResult = false
  PartialLoad = false
  Refine = true
  Relative = true
  Support = -> [Sketch006]
  _Version = 2
FEATURE [PartDesign::Body] Body012  label="PinBody"
  AllowCompound = false
  Group = -> [Sketch060,Pad019,Chamfer017,Binder015]
  Origin = -> Origin039
  Tip = -> Chamfer017
FEATURE [App::Part] Part010  label="AxlePin"
  Group = -> [Body012]
  Origin = -> Origin038
  Placement = pos=(14.4,0,0) rot=(0,0,1;0rad)
FEATURE [PartDesign::SubShapeBinder] Binder016  label="FilamentPathBinder"
  BindCopyOnChange = 0
  BindMode = 0
  ClaimChildren = false
  Context = -> Part011 [Body013.Binder016.]
  Fuse = false
  MakeFace = true
  OffsetFill = false
  OffsetIntersection = false
  OffsetJoinType = 0
  OffsetOpenResult = false
  PartialLoad = false
  Refine = true
  Relative = true
  Support = -> [Sketch006]
  _Version = 2
FEATURE [Sketcher::SketchObject] Sketch062  label="NewTaz Base"
  ArcFitTolerance = 1e-06
  AttachmentOffset = pos=(0,-15.85,10) rot=(1,0,0;1.5708rad)
  AttachmentSupport = -> [XZ_Plane041]
  ExternalGeometry = -> [Binder016]
  FullyConstrained = true
  MakeInternals = false
  MapMode = 3
  Placement = pos=(0,15.85,-10) rot=(1,0,0;4.71239rad)
  sketch-geometry (17):
    g0: LineSegment StartX=-23.75 StartY=76.5 StartZ=0 EndX=-23.75 EndY=-33.5 EndZ=0
    g1: LineSegment StartX=-23.75 StartY=-33.5 StartZ=0 EndX=36.25 EndY=-33.5 EndZ=0
    g2: LineSegment StartX=36.25 StartY=-33.5 StartZ=0 EndX=36.25 EndY=76.5 EndZ=0
    g3: LineSegment StartX=36.25 StartY=76.5 StartZ=0 EndX=-23.75 EndY=76.5 EndZ=0
    g4: Circle CenterX=-18.75 CenterY=56.5 CenterZ=0 NormalX=0 NormalY=0 NormalZ=1 AngleXU=0 Radius=1.6
    g5: Circle CenterX=31.25 CenterY=56.5 CenterZ=0 NormalX=0 NormalY=0 NormalZ=1 AngleXU=0 Radius=1.6
    g6: Circle CenterX=-18.75 CenterY=26.5 CenterZ=0 NormalX=0 NormalY=0 NormalZ=1 AngleXU=0 Radius=1.6
    g7: Circle CenterX=31.25 CenterY=26.5 CenterZ=0 NormalX=0 NormalY=0 NormalZ=1 AngleXU=0 Radius=1.6
    g8: Circle CenterX=-18.75 CenterY=16.5 CenterZ=0 NormalX=0 NormalY=0 NormalZ=1 AngleXU=0 Radius=1.6
    g9: Circle CenterX=-18.75 CenterY=-13.5 CenterZ=0 NormalX=0 NormalY=0 NormalZ=1 AngleXU=0 Radius=1.6
    g10: Circle CenterX=31.25 CenterY=16.5 CenterZ=0 NormalX=0 NormalY=0 NormalZ=1 AngleXU=0 Radius=1.6
    g11: Circle CenterX=31.25 CenterY=-13.5 CenterZ=0 NormalX=0 NormalY=0 NormalZ=1 AngleXU=0 Radius=1.6
    g12: LineSegment [constr] StartX=-18.75 StartY=56.5 StartZ=0 EndX=-18.75 EndY=26.5 EndZ=0
    g13: LineSegment [constr] StartX=-18.75 StartY=16.5 StartZ=0 EndX=-18.75 EndY=-13.5 EndZ=0
    g14: LineSegment [constr] StartX=-18.75 StartY=26.5 StartZ=0 EndX=-18.75 EndY=16.5 EndZ=0
    g15: LineSegment [constr] StartX=6.25 StartY=76.5 StartZ=0 EndX=6.25 EndY=-33.5 EndZ=0
    g16: LineSegment [constr] StartX=-23.75 StartY=21.5 StartZ=0 EndX=36.25 EndY=21.5 EndZ=0
  constraints (39):
    c: Vertical(g0)
    c: Coincident(g0,g1)
    c: Coincident(g1,g2)
    c: DistanceX(g1,g1) = 60
    c: Coincident(g0,g3)
    c: Coincident(g2,g3)
    c: DistanceY(g0,g0) = 110
    c: Horizontal(g1)
    c: Coincident(g12,g4)
    c: Coincident(g12,g6)
    c: Vertical(g12)
    c: Coincident(g13,g8)
    c: Coincident(g13,g9)
    c: Coincident(g14,g6)
    c: Coincident(g14,g8)
    c: Equal(g4,g5)
    c: Equal(g6,g7)
    c: Equal(g8,g10)
    c: Equal(g9,g11)
    c: Equal(g5,g7)
    c: Equal(g7,g10)
    c: Equal(g10,g11)
    c: Diameter(g4) = 3.2
    c: DistanceX(g9,g11) = 50
    c: DistanceY(g10,g7) = 10
    c: DistanceY(g7,g5) = 30
    c: Symmetric(g3,g3,g15)
    c: Symmetric(g1,g1,g15)
    c: Symmetric(g5,g4,g15)
    c: Symmetric(g9,g11,g15)
    c: Symmetric(g8,g10,g15)
    c: Symmetric(g6,g7,g15)
    c: Symmetric(g0,g0,g16)
    c: Symmetric(g2,g2,g16)
    c: Horizontal(g16)
    c: Symmetric(g6,g8,g16)
    c: Symmetric(g11,g5,g16)
    c: DistanceY(g-1,g16) = 21.5
    c: Symmetric(g-3,g-3,g15)
FEATURE [PartDesign::SubShapeBinder] Binder017
  BindCopyOnChange = 0
  BindMode = 0
  ClaimChildren = false
  Context = -> Part011 [Body013.Binder017.]
  Fuse = false
  MakeFace = true
  OffsetFill = false
  OffsetIntersection = false
  OffsetJoinType = 0
  OffsetOpenResult = false
  PartialLoad = false
  Placement = pos=(0,30,0) rot=(0,0,1;0rad)
  Refine = true
  Relative = true
  Support = -> [Sketch062]
  _Version = 2
FEATURE [Sketcher::SketchObject] Sketch063
  ArcFitTolerance = 1e-06
  AttachmentSupport = -> [XZ_Plane043]
  FullyConstrained = true
  MakeInternals = false
  MapMode = 5
  Placement = pos=(0,0,0) rot=(1,0,0;1.5708rad)
  sketch-geometry (2):
    g0: Circle CenterX=0 CenterY=0 CenterZ=0 NormalX=0 NormalY=0 NormalZ=1 AngleXU=0 Radius=2.75
    g1: Circle CenterX=0 CenterY=0 CenterZ=0 NormalX=0 NormalY=0 NormalZ=1 AngleXU=0 Radius=1.5
  constraints (4):
    c: Diameter(g0) = 5.5
    c: Coincident(g0,g-1)
    c: Diameter(g1) = 3
    c: Coincident(g1,g0)
FEATURE [PartDesign::Pad] Pad020
  Direction = (0,-1,2e-16)
  Length = 3
  Length2 = 10
  Placement = pos=(0,0,0) rot=(1,0,0;1.5708rad)
  Profile = -> Sketch063 [Edge1]
  ReferenceAxis = -> Sketch063 [N_Axis]
  Refine = true
  Suppressed = false
  Type = 0
FEATURE [PartDesign::Pad] Pad021
  BaseFeature = -> Pad020
  Direction = (0,-1,2e-16)
  Length = 35
  Length2 = 10
  Placement = pos=(0,0,0) rot=(1,0,0;1.5708rad)
  Profile = -> Sketch063 [Edge2]
  ReferenceAxis = -> Sketch063 [N_Axis]
  Refine = true
  Reversed = true
  Suppressed = false
  Type = 0
FEATURE [PartDesign::Chamfer] Chamfer018
  Angle = 45
  Base = -> Pad021 [Edge3,Edge2]
  BaseFeature = -> Pad021
  ChamferType = 0
  FlipDirection = false
  Placement = pos=(0,0,0) rot=(1,0,0;1.5708rad)
  Refine = true
  Size = 0.2
  Size2 = 1
  SupportTransform = false
  Suppressed = false
  UseAllEdges = false
FEATURE [PartDesign::Body] Body014  label="M35ScrewBody"
  AllowCompound = false
  Group = -> [Sketch063,Pad020,Pad021,Chamfer018]
  Origin = -> Origin043
  Tip = -> Chamfer018
FEATURE [App::Part] Part012  label="M35"
  Group = -> [Body014]
  Origin = -> Origin042
  Placement = pos=(31.25,14.5,-26.5) rot=(0,0,1;0rad)
FEATURE [Sketcher::SketchObject] Sketch064
  ArcFitTolerance = 1e-06
  AttachmentSupport = -> [Binder017]
  ExternalGeometry = -> [Binder017]
  FullyConstrained = true
  MakeInternals = false
  MapMode = 5
  Placement = pos=(0,45.85,-3.6e-15) rot=(0,0.707107,0.707107;3.14159rad)
  sketch-geometry (26):
    g0: LineSegment [constr] StartX=-36.25 StartY=-31.5 StartZ=0 EndX=23.75 EndY=-31.5 EndZ=0
    g1: LineSegment StartX=-36.25 StartY=-31.3 StartZ=0 EndX=23.75 EndY=-31.3 EndZ=0
    g2: LineSegment StartX=23.75 StartY=-31.3 StartZ=0 EndX=23.75 EndY=-21.5 EndZ=0
    g3: LineSegment StartX=23.75 StartY=-21.5 StartZ=0 EndX=18.45 EndY=-21.5 EndZ=0
    g4: LineSegment StartX=18.45 StartY=-21.5 StartZ=0 EndX=18.45 EndY=-1.5 EndZ=0
    g5: LineSegment StartX=18.45 StartY=39.5 StartZ=0 EndX=-23.05 EndY=39.5 EndZ=0
    g6: LineSegment StartX=-23.05 StartY=39.5 StartZ=0 EndX=-23.05 EndY=8.5 EndZ=0
    g7: LineSegment StartX=-23.05 StartY=8.5 StartZ=0 EndX=-36.25 EndY=8.5 EndZ=0
    g8: LineSegment StartX=-36.25 StartY=8.5 StartZ=0 EndX=-36.25 EndY=-1.5 EndZ=0
    g9: LineSegment StartX=-36.25 StartY=-1.5 StartZ=0 EndX=-23.05 EndY=-1.5 EndZ=0
    g10: LineSegment StartX=-23.05 StartY=-1.5 StartZ=0 EndX=-23.05 EndY=-21.5 EndZ=0
    g11: LineSegment StartX=-23.05 StartY=-21.5 StartZ=0 EndX=-36.25 EndY=-21.5 EndZ=0
    g12: LineSegment StartX=-36.25 StartY=-21.5 StartZ=0 EndX=-36.25 EndY=-31.3 EndZ=0
    g13: LineSegment [constr] StartX=-23.05 StartY=-21.5 StartZ=0 EndX=18.45 EndY=-21.5 EndZ=0
    g14: LineSegment [constr] StartX=-23.05 StartY=8.5 StartZ=0 EndX=-23.05 EndY=-1.5 EndZ=0
    g15: LineSegment [constr] StartX=-31.25 StartY=3.5 StartZ=0 EndX=-36.25 EndY=3.5 EndZ=0
    g16: Circle CenterX=-31.25 CenterY=-26.5 CenterZ=0 NormalX=0 NormalY=0 NormalZ=1 AngleXU=0 Radius=1.7
    g17: Circle CenterX=18.75 CenterY=-26.5 CenterZ=0 NormalX=0 NormalY=0 NormalZ=1 AngleXU=0 Radius=1.7
    g18: Circle CenterX=-31.25 CenterY=3.5 CenterZ=0 NormalX=0 NormalY=0 NormalZ=1 AngleXU=0 Radius=1.7
    g19: LineSegment [constr] StartX=18.45 StartY=8.5 StartZ=0 EndX=23.75 EndY=8.5 EndZ=0
    g20: LineSegment [constr] StartX=23.75 StartY=8.5 StartZ=0 EndX=23.75 EndY=-1.5 EndZ=0
    g21: LineSegment [constr] StartX=23.75 StartY=-1.5 StartZ=0 EndX=18.45 EndY=-1.5 EndZ=0
    g22: LineSegment StartX=18.45 StartY=8.5 StartZ=0 EndX=18.45 EndY=39.5 EndZ=0
    g23: LineSegment StartX=18.45 StartY=8.5 StartZ=0 EndX=18.45 EndY=-1.5 EndZ=0
    g24: LineSegment [constr] StartX=-23.05 StartY=8.5 StartZ=0 EndX=18.45 EndY=8.5 EndZ=0
    g25: LineSegment [constr] StartX=-23.05 StartY=-1.5 StartZ=0 EndX=18.45 EndY=-1.5 EndZ=0
  constraints (68):
    c: Symmetric(g-3,g-3,g0)
    c: Symmetric(g-4,g-4,g0)
    c: PointOnObject(g1,g-3)
    c: PointOnObject(g1,g-4)
    c: Horizontal(g1)
    c: Coincident(g1,g2)
    c: PointOnObject(g2,g-4)
    c: Coincident(g2,g3)
    c: Horizontal(g3)
    c: Coincident(g3,g4)
    c: Vertical(g4)
    c: Coincident(g22,g5)
    c: Horizontal(g5)
    c: Coincident(g5,g6)
    c: Vertical(g6)
    c: Coincident(g6,g7)
    c: PointOnObject(g7,g-3)
    c: Horizontal(g7)
    c: Coincident(g7,g8)
    c: PointOnObject(g8,g-3)
    c: Coincident(g8,g9)
    c: Horizontal(g9)
    c: Coincident(g9,g10)
    c: Vertical(g10)
    c: Coincident(g10,g11)
    c: PointOnObject(g11,g-3)
    c: Horizontal(g11)
    c: Coincident(g11,g12)
    c: Coincident(g12,g1)
    c: Coincident(g14,g6)
    c: Coincident(g14,g9)
    c: Vertical(g14)
    c: Coincident(g13,g3)
    c: Horizontal(g13)
    c: Coincident(g13,g10)
    c: DistanceY(g0,g1) = 0.2
    c: DistanceY(g8,g8) = 10
    c: Coincident(g15,g-5)
    c: Symmetric(g8,g8,g15)
    c: Horizontal(g15)
    c: DistanceY(g0,g2) = 10
    c: DistanceX(g5,g5) = 41.5
    c: DistanceX(g11,g11) = 13.2
    c: DistanceY(g11,g5) = 61
    c: Coincident(g16,g-6)
    c: Coincident(g17,g-7)
    c: Coincident(g18,g15)
    c: Diameter(g18) = 3.4
    c: PointOnObject(g19,g-4)
    c: Coincident(g19,g20)
    c: PointOnObject(g20,g-4)
    c: Coincident(g20,g21)
    c: Coincident(g4,g21)
    c: Coincident(g24,g6)
    c: Coincident(g24,g19)
    c: Horizontal(g24)
    c: Coincident(g25,g9)
    c: Coincident(g25,g23)
    c: Horizontal(g25)
    c: Coincident(g23,g22)
    c: Coincident(g22,g19)
    c: Coincident(g4,g23)
    c: Vertical(g22)
    c: Perpendicular(g4,g21)
    c: Perpendicular(g20,g19)
    c: Vertical(g23)
    c: Equal(g18,g16)
    c: Equal(g17,g16)
FEATURE [PartDesign::Pad] Pad022  label="PlateBase"
  Direction = (0,1,-2e-16)
  Length = 24
  Length2 = 10
  Placement = pos=(0,30,0) rot=(0,0,1;0rad)
  Profile = -> Sketch064
  ReferenceAxis = -> Sketch064 [N_Axis]
  Refine = true
  Reversed = true
  Suppressed = false
  Type = 0
FEATURE [Sketcher::SketchObject] Sketch065
  ArcFitTolerance = 1e-06
  ExternalGeometry = -> [Pad022]
  FullyConstrained = true
  MakeInternals = false
  MapMode = 5
  Placement = pos=(23.05,30,0) rot=(0.57735,0.57735,0.57735;2.0944rad)
  sketch-geometry (9):
    g0: LineSegment StartX=15.85 StartY=8.5 StartZ=0 EndX=15.85 EndY=39.5 EndZ=0
    g1: LineSegment StartX=15.85 StartY=39.5 StartZ=0 EndX=-1.95 EndY=39.5 EndZ=0
    g2: LineSegment StartX=-1.95 StartY=39.5 StartZ=0 EndX=-1.95 EndY=8.5 EndZ=0
    g3: LineSegment StartX=-1.95 StartY=8.5 StartZ=0 EndX=15.85 EndY=8.5 EndZ=0
    g4: LineSegment StartX=15.85 StartY=-21.5 StartZ=0 EndX=15.85 EndY=-1.5 EndZ=0
    g5: LineSegment StartX=15.85 StartY=-1.5 StartZ=0 EndX=-1.95 EndY=-1.5 EndZ=0
    g6: LineSegment StartX=-1.95 StartY=-1.5 StartZ=0 EndX=-1.95 EndY=-21.5 EndZ=0
    g7: LineSegment StartX=-1.95 StartY=-21.5 StartZ=0 EndX=15.85 EndY=-21.5 EndZ=0
    g8: LineSegment [constr] StartX=-1.95 StartY=8.5 StartZ=0 EndX=-1.95 EndY=-1.5 EndZ=0
  constraints (22):
    c: Coincident(g0,g1)
    c: Coincident(g1,g2)
    c: Coincident(g2,g3)
    c: Coincident(g3,g0)
    c: Vertical(g2)
    c: Horizontal(g1)
    c: Horizontal(g3)
    c: Coincident(g0,g-4)
    c: Coincident(g4,g5)
    c: Coincident(g5,g6)
    c: Coincident(g6,g7)
    c: Coincident(g7,g4)
    c: Vertical(g6)
    c: Horizontal(g5)
    c: Horizontal(g7)
    c: Coincident(g4,g-3)
    c: Coincident(g4,g-3)
    c: Coincident(g0,g-4)
    c: Coincident(g8,g2)
    c: Coincident(g8,g5)
    c: Vertical(g8)
    c: DistanceX(g-5,g1) = 6.2
FEATURE [PartDesign::Pocket] Pocket031  label="CarveSupportsPk"
  BaseFeature = -> Pad022
  Direction = (-1,-1e-16,1e-16)
  Length = 45
  Length2 = 5
  Placement = pos=(0,30,0) rot=(0,0,1;0rad)
  Profile = -> Sketch065
  ReferenceAxis = -> Sketch065 [N_Axis]
  Refine = true
  Suppressed = false
  Type = 0
FEATURE [Sketcher::SketchObject] Sketch066
  ArcFitTolerance = 1e-06
  AttachmentSupport = -> [Pocket031]
  ExternalGeometry = -> [Pocket031]
  FullyConstrained = true
  MakeInternals = false
  MapMode = 5
  Placement = pos=(0,45.85,0) rot=(0,0.707107,0.707107;3.14159rad)
  sketch-geometry (12):
    g0: LineSegment StartX=-19.05 StartY=-1.5 StartZ=0 EndX=18.45 EndY=-1.5 EndZ=0
    g1: LineSegment StartX=18.45 StartY=-1.5 StartZ=0 EndX=18.45 EndY=8.5 EndZ=0
    g2: LineSegment StartX=18.45 StartY=8.5 StartZ=0 EndX=-19.05 EndY=8.5 EndZ=0
    g3: LineSegment StartX=-19.05 StartY=8.5 StartZ=0 EndX=-19.05 EndY=-1.5 EndZ=0
    g4: LineSegment [constr] StartX=-23.05 StartY=8.5 StartZ=0 EndX=-19.05 EndY=8.5 EndZ=0
    g5: LineSegment StartX=-19.05 StartY=-21.5 StartZ=0 EndX=-19.05 EndY=-31.3 EndZ=0
    g6: LineSegment StartX=-19.05 StartY=-31.3 StartZ=0 EndX=6.55 EndY=-31.3 EndZ=0
    g7: LineSegment StartX=6.55 StartY=-31.3 StartZ=0 EndX=6.55 EndY=-21.5 EndZ=0
    g8: LineSegment StartX=6.55 StartY=-21.5 StartZ=0 EndX=-19.05 EndY=-21.5 EndZ=0
    g9: LineSegment [constr] StartX=-19.05 StartY=-1.5 StartZ=0 EndX=-19.05 EndY=-21.5 EndZ=0
    g10: LineSegment [constr] StartX=-36.25 StartY=-31.3 StartZ=0 EndX=-19.05 EndY=-31.3 EndZ=0
    g11: LineSegment [constr] StartX=6.55 StartY=-31.3 StartZ=0 EndX=23.75 EndY=-31.3 EndZ=0
  constraints (31):
    c: Coincident(g0,g1)
    c: Coincident(g1,g2)
    c: Coincident(g2,g3)
    c: Coincident(g3,g0)
    c: Horizontal(g2)
    c: Vertical(g1)
    c: Vertical(g3)
    c: Coincident(g4,g-5)
    c: Coincident(g4,g2)
    c: PointOnObject(g0,g-7)
    c: PointOnObject(g0,g-7)
    c: Coincident(g1,g-6)
    c: DistanceX(g4,g4) = 4
    c: Coincident(g5,g6)
    c: Coincident(g6,g7)
    c: Coincident(g7,g8)
    c: Coincident(g8,g5)
    c: Vertical(g5)
    c: Vertical(g7)
    c: Horizontal(g6)
    c: Horizontal(g8)
    c: PointOnObject(g5,g-8)
    c: PointOnObject(g6,g-9)
    c: Coincident(g9,g0)
    c: Coincident(g9,g5)
    c: Vertical(g9)
    c: Coincident(g10,g-9)
    c: Coincident(g10,g5)
    c: Coincident(g11,g6)
    c: Coincident(g11,g-9)
    c: Equal(g10,g11)
FEATURE [PartDesign::Pocket] Pocket032  label="MidSupportCutoutPk"
  BaseFeature = -> Pocket031
  Direction = (0,-1,2e-16)
  Length = 0
  Length2 = 5
  Placement = pos=(0,30,0) rot=(0,0,1;0rad)
  Profile = -> Sketch066
  ReferenceAxis = -> Sketch066 [N_Axis]
  Refine = true
  Suppressed = false
  Type = 3
  UpToFace = -> Pocket031 [Face14]
FEATURE [PartDesign::SubShapeBinder] Binder018
  BindCopyOnChange = 0
  BindMode = 0
  ClaimChildren = false
  Context = -> Part011 [Body013.Binder018.]
  Fuse = false
  MakeFace = true
  OffsetFill = false
  OffsetIntersection = false
  OffsetJoinType = 0
  OffsetOpenResult = false
  PartialLoad = false
  Refine = true
  Relative = true
  Support = -> [Sketch014]
  _Version = 2
FEATURE [Sketcher::SketchObject] Sketch067  label="BaseHolesSk"
  ArcFitTolerance = 1e-06
  AttachmentSupport = -> [Pocket032]
  ExternalGeometry = -> [Binder018]
  FullyConstrained = true
  MakeInternals = false
  MapMode = 5
  Placement = pos=(0,28.05,0) rot=(0,0.707107,0.707107;3.14159rad)
  sketch-geometry (6):
    g0: Circle CenterX=12 CenterY=-15 CenterZ=0 NormalX=0 NormalY=0 NormalZ=1 AngleXU=0 Radius=1.7
    g1: Circle CenterX=3 CenterY=-15 CenterZ=0 NormalX=0 NormalY=0 NormalZ=1 AngleXU=0 Radius=1.7
    g2: Circle CenterX=-18.8 CenterY=-17.2 CenterZ=0 NormalX=0 NormalY=0 NormalZ=1 AngleXU=0 Radius=1.7
    g3: Circle CenterX=3 CenterY=15 CenterZ=0 NormalX=0 NormalY=0 NormalZ=1 AngleXU=0 Radius=1.7
    g4: Circle CenterX=-16.6 CenterY=33 CenterZ=0 NormalX=0 NormalY=0 NormalZ=1 AngleXU=0 Radius=1.7
    g5: Circle CenterX=12 CenterY=33 CenterZ=0 NormalX=0 NormalY=0 NormalZ=1 AngleXU=0 Radius=1.7
  constraints (12):
    c: Coincident(g0,g-7)
    c: Equal(g0,g-7)
    c: Coincident(g1,g-8)
    c: Equal(g1,g-8)
    c: Coincident(g2,g-9)
    c: Equal(g2,g-9)
    c: Coincident(g3,g-6)
    c: Equal(g3,g-6)
    c: Coincident(g4,g-5)
    c: Equal(g4,g-5)
    c: Coincident(g5,g-3)
    c: Equal(g5,g-3)
FEATURE [Sketcher::SketchObject] Sketch068  label="BearingSk"
  ArcFitTolerance = 1e-06
  AttachmentSupport = -> [Pad022]
  FullyConstrained = true
  MakeInternals = false
  MapMode = 5
  Placement = pos=(0,21.85,0) rot=(1,0,0;1.5708rad)
  sketch-geometry (3):
    g0: Circle CenterX=0 CenterY=0 CenterZ=0 NormalX=0 NormalY=0 NormalZ=1 AngleXU=0 Radius=6.625
    g1: Circle CenterX=0 CenterY=0 CenterZ=0 NormalX=0 NormalY=0 NormalZ=1 AngleXU=0 Radius=7.6
    g2: Circle CenterX=0 CenterY=0 CenterZ=0 NormalX=0 NormalY=0 NormalZ=1 AngleXU=0 Radius=2.7
  constraints (6):
    c: Coincident(g0,g-1)
    c: Coincident(g1,g0)
    c: Diameter(g1) = 15.2
    c: Diameter(g0) = 13.25
    c: Coincident(g2,g0)
    c: Diameter(g2) = 5.4
FEATURE [PartDesign::Hole] Hole012  label="FilamentPathOut3mm"
  BaseFeature = -> Pocket024
  CustomThreadClearance = 0
  Depth = 100
  DepthType = 0
  Diameter = 3
  DrillForDepth = false
  DrillPoint = 1
  DrillPointAngle = 118
  HoleCutCountersinkAngle = 90
  HoleCutCustomValues = false
  HoleCutDepth = 0
  HoleCutDiameter = 6.1
  HoleCutType = 0
  ModelThread = false
  Placement = pos=(0,0,0) rot=(1,0,0;1.5708rad)
  Profile = -> Sketch048 [Edge1]
  Refine = true
  Suppressed = false
  Tapered = false
  TaperedAngle = 90
  ThreadClass = 0
  ThreadDepth = 100
  ThreadDepthType = 0
  ThreadDirection = 0
  ThreadFit = 0
  ThreadSize = 0
  ThreadType = 0
  Threaded = false
  UseCustomThreadClearance = false
FEATURE [PartDesign::Hole] Hole013  label="4mmPtfeHole"
  BaseFeature = -> Hole012
  CustomThreadClearance = 0
  Depth = 10
  DepthType = 0
  Diameter = 4.3
  DrillForDepth = false
  DrillPoint = 1
  DrillPointAngle = 118
  HoleCutCountersinkAngle = 90
  HoleCutCustomValues = false
  HoleCutDepth = 0
  HoleCutDiameter = 6.1
  HoleCutType = 0
  ModelThread = false
  Placement = pos=(0,0,0) rot=(1,0,0;1.5708rad)
  Profile = -> Hole012 [Edge116]
  Refine = true
  Reversed = true
  Suppressed = false
  Tapered = false
  TaperedAngle = 90
  ThreadClass = 0
  ThreadDepth = 10
  ThreadDepthType = 0
  ThreadDirection = 0
  ThreadFit = 0
  ThreadSize = 0
  ThreadType = 0
  Threaded = false
  UseCustomThreadClearance = false
FEATURE [PartDesign::Hole] Hole014  label="6mmPtfeHole"
  BaseFeature = -> Hole013
  CustomThreadClearance = 0
  Depth = 5
  DepthType = 0
  Diameter = 6
  DrillForDepth = false
  DrillPoint = 1
  DrillPointAngle = 118
  HoleCutCountersinkAngle = 90
  HoleCutCustomValues = false
  HoleCutDepth = 0
  HoleCutDiameter = 6.1
  HoleCutType = 0
  ModelThread = false
  Placement = pos=(0,0,0) rot=(1,0,0;1.5708rad)
  Profile = -> Hole013 [Edge116]
  Refine = true
  Reversed = true
  Suppressed = false
  Tapered = false
  TaperedAngle = 90
  ThreadClass = 0
  ThreadDepth = 5
  ThreadDepthType = 0
  ThreadDirection = 0
  ThreadFit = 0
  ThreadSize = 0
  ThreadType = 0
  Threaded = false
  UseCustomThreadClearance = false
FEATURE [Sketcher::SketchObject] Sketch069
  ArcFitTolerance = 1e-06
  AttachmentSupport = -> [Pocket024]
  ExternalGeometry = -> [Binder010,Sketch036,Hole014]
  FullyConstrained = true
  MakeInternals = false
  MapMode = 5
  Placement = pos=(0,-1.1e-14,-31.3) rot=(1,0,0;3.14159rad)
  sketch-geometry (6):
    g0: LineSegment [constr] StartX=36.25 StartY=-9.7 StartZ=0 EndX=-23.75 EndY=-9.7 EndZ=0
    g1: LineSegment [constr] StartX=6.25 StartY=-9.7 StartZ=0 EndX=6.25 EndY=-22 EndZ=0
    g2: LineSegment StartX=-23.75 StartY=0 StartZ=0 EndX=-23.75 EndY=-9.7 EndZ=0
    g3: LineSegment StartX=-23.75 StartY=-9.7 StartZ=0 EndX=36.25 EndY=-9.7 EndZ=0
    g4: LineSegment StartX=36.25 StartY=-9.7 StartZ=0 EndX=36.25 EndY=0 EndZ=0
    g5: LineSegment StartX=36.25 StartY=0 StartZ=0 EndX=-23.75 EndY=0 EndZ=0
  constraints (16):
    c: Horizontal(g0)
    c: Symmetric(g0,g0,g1)
    c: Symmetric(g1,g1,g-3)
    c: Vertical(g1)
    c: PointOnObject(g1,g-4)
    c: PointOnObject(g0,g-5)
    c: Coincident(g2,g3)
    c: Coincident(g3,g4)
    c: Coincident(g4,g5)
    c: Coincident(g5,g2)
    c: Vertical(g2)
    c: Vertical(g4)
    c: Horizontal(g3)
    c: Horizontal(g5)
    c: Coincident(g2,g-5)
    c: Coincident(g3,g0)
FEATURE [PartDesign::Pocket] Pocket037  label="SupportCutOut"
  BaseFeature = -> Hole014
  Direction = (0,0,1)
  Length = 0
  Length2 = 5
  Placement = pos=(0,0,0) rot=(1,0,0;1.5708rad)
  Profile = -> Sketch069
  ReferenceAxis = -> Sketch069 [N_Axis]
  Refine = true
  Suppressed = false
  Type = 3
  UpToFace = -> Hole014 [Face35]
FEATURE [Sketcher::SketchObject] Sketch070  label="MountHolesSk"
  ArcFitTolerance = 1e-06
  AttachmentSupport = -> [Pocket037]
  ExternalGeometry = -> [Fillet021]
  FullyConstrained = true
  MakeInternals = false
  MapMode = 5
  Placement = pos=(0,9.7,-2.1e-15) rot=(1,0,0;1.5708rad)
  sketch-geometry (4):
    g0: LineSegment [constr] StartX=-23.75 StartY=-26.5 StartZ=0 EndX=36.25 EndY=-26.5 EndZ=0
    g1: Circle CenterX=-18.75 CenterY=-26.5 CenterZ=0 NormalX=0 NormalY=0 NormalZ=1 AngleXU=0 Radius=1.6
    g2: Circle CenterX=31.25 CenterY=-26.5 CenterZ=0 NormalX=0 NormalY=0 NormalZ=1 AngleXU=0 Radius=1.6
    g3: GeomPoint [constr] X=6.25 Y=-26.5 Z=0
  constraints (10):
    c: PointOnObject(g1,g0)
    c: DistanceY(g0,g-3) = 5
    c: Diameter(g2) = 3.2
    c: Equal(g1,g2)
    c: DistanceX(g1,g2) = 50
    c: Symmetric(g0,g0,g3)
    c: Symmetric(g1,g2,g3)
    c: Horizontal(g0)
    c: PointOnObject(g0,g-3)
    c: PointOnObject(g0,g-4)
FEATURE [PartDesign::Hole] Hole015  label="MountHoles"
  BaseFeature = -> Pocket037
  CustomThreadClearance = 0
  Depth = 20
  DepthType = 0
  Diameter = 3.4
  DrillForDepth = false
  DrillPoint = 1
  DrillPointAngle = 118
  HoleCutCountersinkAngle = 90
  HoleCutCustomValues = false
  HoleCutDepth = 5
  HoleCutDiameter = 6.1
  HoleCutType = 1
  ModelThread = false
  Placement = pos=(0,0,0) rot=(1,0,0;1.5708rad)
  Profile = -> Sketch070
  Refine = true
  Suppressed = false
  Tapered = false
  TaperedAngle = 90
  ThreadClass = 0
  ThreadDepth = 20
  ThreadDepthType = 0
  ThreadDirection = 0
  ThreadFit = 0
  ThreadSize = 9
  ThreadType = 1
  Threaded = false
  UseCustomThreadClearance = false
FEATURE [PartDesign::Fillet] Fillet051
  Base = -> Hole015 [Edge119,Edge125]
  BaseFeature = -> Hole015
  Placement = pos=(0,0,0) rot=(1,0,0;1.5708rad)
  Radius = 3
  Refine = true
  SupportTransform = false
  Suppressed = false
  UseAllEdges = false
FEATURE [PartDesign::Fillet] Fillet052
  Base = -> Fillet051 [Edge46,Edge42,Edge37,Edge65]
  BaseFeature = -> Fillet051
  Placement = pos=(0,0,0) rot=(1,0,0;1.5708rad)
  Radius = 1
  Refine = true
  SupportTransform = false
  Suppressed = false
  UseAllEdges = false
FEATURE [PartDesign::Body] Body007  label="Body-Lower"
  AllowCompound = false
  Group = -> [Sketch036,Binder009,Pad008,Fillet021,Fillet022,Binder010,Sketch037,Sketch038,Pocket018,Pocket019,Pad009,Sketch039,Pocket020,Fillet023,Fillet024,Fillet025,Sketch048,Sketch049,Pocket024,Hole012,Hole013,Hole014,Sketch069,Pocket037,Sketch070,Hole015,Fillet051,Fillet052]
  Origin = -> Origin028
  Tip = -> Fillet052
FEATURE [App::Part] Part005  label="BodyLower"
  Group = -> [Body007]
  Origin = -> Origin027
FEATURE [App::DocumentObjectGroup] Group003  label="Optional"
  Group = -> [Part010,Part008,Part004]
FEATURE [PartDesign::Hole] Hole016
  BaseFeature = -> Pocket032
  CustomThreadClearance = 0
  Depth = 25
  DepthType = 0
  Diameter = 3.4
  DrillForDepth = false
  DrillPoint = 1
  DrillPointAngle = 118
  HoleCutCountersinkAngle = 90
  HoleCutCustomValues = false
  HoleCutDepth = 2.4
  HoleCutDiameter = 6.1
  HoleCutType = 1
  ModelThread = false
  Placement = pos=(0,30,0) rot=(0,0,1;0rad)
  Profile = -> Sketch067
  Refine = true
  Suppressed = false
  Tapered = false
  TaperedAngle = 90
  ThreadClass = 0
  ThreadDepth = 25
  ThreadDepthType = 0
  ThreadDirection = 0
  ThreadFit = 0
  ThreadSize = 9
  ThreadType = 1
  Threaded = false
  UseCustomThreadClearance = false
FEATURE [PartDesign::Pocket] Pocket034  label="AxleBearing"
  BaseFeature = -> Hole016
  Direction = (0,1,-2e-16)
  Length = 4.2
  Length2 = 5
  Placement = pos=(0,30,0) rot=(0,0,1;0rad)
  Profile = -> Sketch068 [Edge1]
  ReferenceAxis = -> Sketch068 [N_Axis]
  Refine = true
  Suppressed = false
  Type = 0
FEATURE [PartDesign::Pocket] Pocket035  label="AxleBearingFlangePk"
  BaseFeature = -> Pocket034
  Direction = (0,1,-2e-16)
  Length = 1.2
  Length2 = 5
  Placement = pos=(0,30,0) rot=(0,0,1;0rad)
  Profile = -> Sketch068 [Edge2]
  ReferenceAxis = -> Sketch068 [N_Axis]
  Refine = true
  Suppressed = false
  Type = 0
FEATURE [PartDesign::Pocket] Pocket036  label="AxlePk"
  BaseFeature = -> Pocket035
  Direction = (0,1,-2e-16)
  Length = 7
  Length2 = 5
  Placement = pos=(0,30,0) rot=(0,0,1;0rad)
  Profile = -> Sketch068 [Edge3]
  ReferenceAxis = -> Sketch068 [N_Axis]
  Refine = true
  Suppressed = false
  Type = 0
FEATURE [PartDesign::Hole] Hole017  label="FrontScrewCounterbore"
  BaseFeature = -> Pocket036
  CustomThreadClearance = 0
  Depth = 3.4
  DepthType = 0
  Diameter = 6.1
  DrillForDepth = false
  DrillPoint = 0
  DrillPointAngle = 118
  HoleCutCountersinkAngle = 90
  HoleCutCustomValues = false
  HoleCutDepth = 0
  HoleCutDiameter = 6.2
  HoleCutType = 0
  ModelThread = false
  Placement = pos=(0,30,0) rot=(0,0,1;0rad)
  Profile = -> Pocket036 [Edge44]
  Refine = true
  Reversed = true
  Suppressed = false
  Tapered = false
  TaperedAngle = 90
  ThreadClass = 0
  ThreadDepth = 3.4
  ThreadDepthType = 0
  ThreadDirection = 0
  ThreadFit = 0
  ThreadSize = 0
  ThreadType = 0
  Threaded = false
  UseCustomThreadClearance = false
FEATURE [PartDesign::Fillet] Fillet048
  Base = -> Hole017 [Edge51,Edge67,Edge56,Edge46,Edge50,Edge47,Edge65,Edge53]
  BaseFeature = -> Hole017
  Placement = pos=(0,30,0) rot=(0,0,1;0rad)
  Radius = 3
  Refine = true
  SupportTransform = false
  Suppressed = false
  UseAllEdges = false
FEATURE [PartDesign::Fillet] Fillet049
  Base = -> Fillet048 [Edge36]
  BaseFeature = -> Fillet048
  Placement = pos=(0,30,0) rot=(0,0,1;0rad)
  Radius = 6.5
  Refine = true
  SupportTransform = false
  Suppressed = false
  UseAllEdges = false
FEATURE [PartDesign::Fillet] Fillet050
  Base = -> Fillet049 [Edge26,Edge57,Edge55,Edge53,Edge49]
  BaseFeature = -> Fillet049
  Placement = pos=(0,30,0) rot=(0,0,1;0rad)
  Radius = 1
  Refine = true
  SupportTransform = false
  Suppressed = false
  UseAllEdges = false
FEATURE [Sketcher::SketchObject] Sketch071
  ArcFitTolerance = 1e-06
  AttachmentSupport = -> [Fillet050]
  ExternalGeometry = -> [Fillet050]
  FullyConstrained = true
  MakeInternals = false
  MapMode = 5
  Placement = pos=(0,28.05,0) rot=(0,0.707107,0.707107;3.14159rad)
  sketch-geometry (4):
    g0: LineSegment StartX=-19.05 StartY=-24.5 StartZ=0 EndX=-19.05 EndY=-30.3 EndZ=0
    g1: LineSegment StartX=-19.05 StartY=-30.3 StartZ=0 EndX=6.55 EndY=-30.3 EndZ=0
    g2: LineSegment StartX=6.55 StartY=-30.3 StartZ=0 EndX=6.55 EndY=-24.5 EndZ=0
    g3: LineSegment StartX=6.55 StartY=-24.5 StartZ=0 EndX=-19.05 EndY=-24.5 EndZ=0
  constraints (10):
    c: Coincident(g0,g1)
    c: Coincident(g1,g2)
    c: Coincident(g2,g3)
    c: Coincident(g3,g0)
    c: Vertical(g0)
    c: Vertical(g2)
    c: Horizontal(g1)
    c: Horizontal(g3)
    c: Coincident(g0,g-3)
    c: Coincident(g1,g-4)
FEATURE [PartDesign::Pad] Pad025  label="SupportPad"
  BaseFeature = -> Fillet050
  Direction = (0,1,-2e-16)
  Length = 5
  Length2 = 10
  Placement = pos=(0,30,0) rot=(0,0,1;0rad)
  Profile = -> Sketch071
  ReferenceAxis = -> Sketch071 [N_Axis]
  Refine = true
  Suppressed = false
  Type = 0
FEATURE [PartDesign::Pad] Pad023  label="BearingCounterIsolation"
  BaseFeature = -> Pad025
  Direction = (0,1,0)
  Length = 0.2
  Length2 = 10
  Placement = pos=(0,30,0) rot=(0,0,1;0rad)
  Profile = -> Fillet050 [Edge86]
  Refine = true
  Suppressed = false
  Type = 0
FEATURE [PartDesign::Pad] Pad024  label="BearingCounterIsolation2"
  BaseFeature = -> Pad023
  Direction = (0,1,0)
  Length = 0.2
  Length2 = 10
  Placement = pos=(0,30,0) rot=(0,0,1;0rad)
  Profile = -> Pad023 [Edge159]
  Refine = true
  Suppressed = false
  Type = 0
FEATURE [PartDesign::Pad] Pad026  label="BaseCounterIsolation"
  BaseFeature = -> Pad024
  Direction = (0,1,0)
  Length = 0.2
  Length2 = 10
  Placement = pos=(0,30,0) rot=(0,0,1;0rad)
  Profile = -> Pad024 [Edge151]
  Refine = true
  Suppressed = false
  Type = 0
FEATURE [PartDesign::Body] Body013  label="MountPlate"
  AllowCompound = false
  Group = -> [Binder016,Sketch062,Binder017,Sketch064,Pad022,Sketch065,Pocket031,Sketch066,Pocket032,Binder018,Sketch067,Sketch068,Hole016,Pocket034,Pocket035,Pocket036,Hole017,Fillet048,Fillet049,Fillet050,Sketch071,Pad025,Pad023,Pad024,Pad026]
  Origin = -> Origin041
  Tip = -> Fillet050
FEATURE [App::Part] Part011  label="BackPlateDirectTaz"
  Group = -> [Body013]
  Origin = -> Origin040
FEATURE [App::DocumentObjectGroup] Group001  label="Extruder"
  Group = -> [Part,Part003,Part005,Part006,Part007,Part011]
FEATURE [Sketcher::SketchObject] Sketch072
  ArcFitTolerance = 1e-06
  AttachmentSupport = -> [XZ_Plane045]
  FullyConstrained = true
  MakeInternals = false
  MapMode = 5
  Placement = pos=(0,0,0) rot=(1,0,0;1.5708rad)
  sketch-geometry (2):
    g0: Circle CenterX=0 CenterY=0 CenterZ=0 NormalX=0 NormalY=0 NormalZ=1 AngleXU=0 Radius=1.5
    g1: Circle CenterX=0 CenterY=0 CenterZ=0 NormalX=0 NormalY=0 NormalZ=1 AngleXU=0 Radius=2.75
  constraints (4):
    c: Coincident(g0,g-1)
    c: Coincident(g1,g0)
    c: Diameter(g1) = 5.5
    c: Diameter(g0) = 3
FEATURE [PartDesign::Pad] Pad027
  Direction = (0,-1,2e-16)
  Length = 25
  Length2 = 10
  Placement = pos=(0,0,0) rot=(1,0,0;1.5708rad)
  Profile = -> Sketch072 [Edge1]
  ReferenceAxis = -> Sketch072 [N_Axis]
  Refine = true
  Reversed = true
  Suppressed = false
  Type = 0
FEATURE [PartDesign::Pad] Pad028
  BaseFeature = -> Pad027
  Direction = (0,-1,2e-16)
  Length = 3
  Length2 = 10
  Placement = pos=(0,0,0) rot=(1,0,0;1.5708rad)
  Profile = -> Sketch072 [Edge2]
  ReferenceAxis = -> Sketch072 [N_Axis]
  Refine = true
  Suppressed = false
  Type = 0
FEATURE [PartDesign::Chamfer] Chamfer019
  Angle = 45
  Base = -> Pad028 [Edge6,Edge3,Edge4]
  BaseFeature = -> Pad028
  ChamferType = 0
  FlipDirection = false
  Placement = pos=(0,0,0) rot=(1,0,0;1.5708rad)
  Refine = true
  Size = 0.5
  Size2 = 1
  SupportTransform = false
  Suppressed = false
  UseAllEdges = false
FEATURE [PartDesign::Body] Body015
  AllowCompound = false
  Group = -> [Sketch072,Pad027,Pad028,Chamfer019]
  Origin = -> Origin045
  Tip = -> Chamfer019
FEATURE [App::Part] Part013  label="M25"
  Group = -> [Body015]
  Origin = -> Origin044
  Placement = pos=(31.25,24.75,3.5) rot=(0,0,1;0rad)
FEATURE [App::DocumentObjectGroup] Group  label="Reference"
  Group = -> [_0t_pulley_no_flange001,_0t_pulley_no_flange,Part002,Part009,Part012,Part013]
